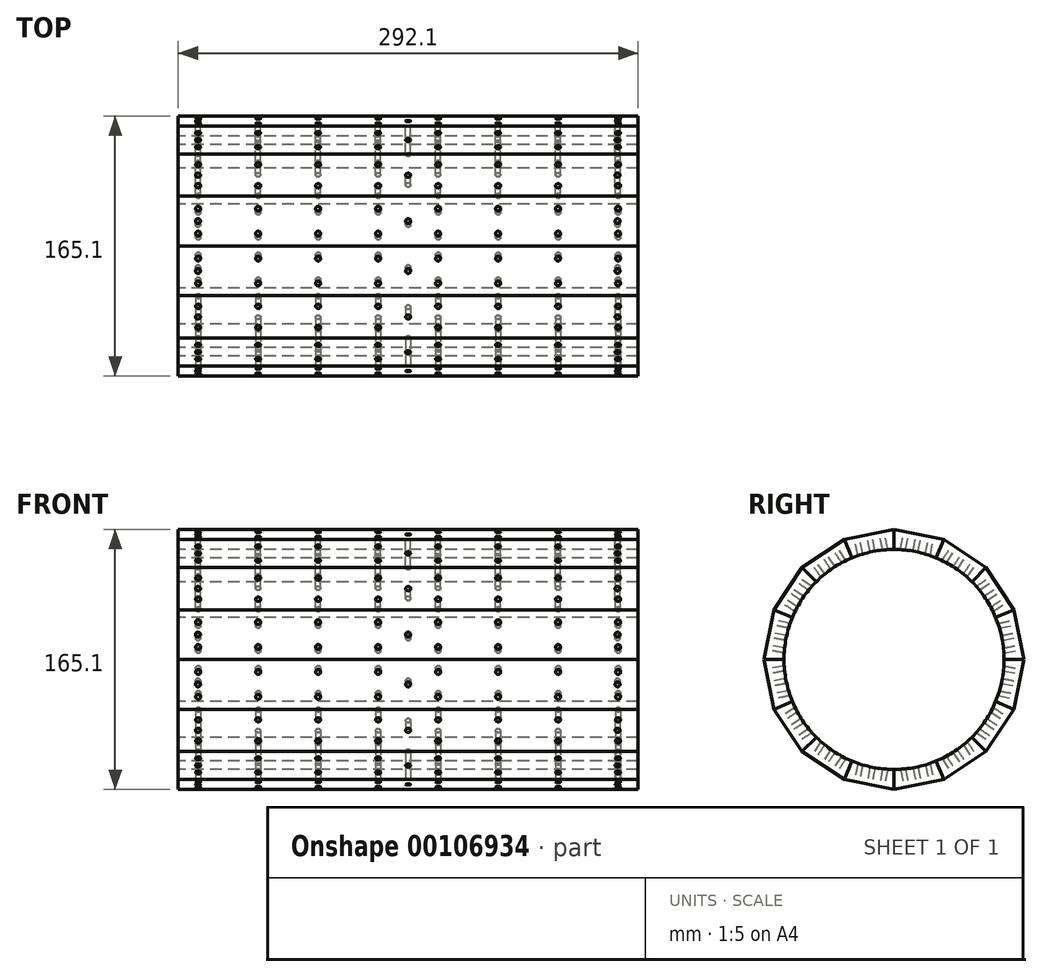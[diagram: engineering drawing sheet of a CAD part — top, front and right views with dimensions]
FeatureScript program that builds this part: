
annotation { "Feature Type Name" : "Feature", "Feature Type Description" : "" }
export const myFeature = defineFeature(function(context is Context, id is Id, definition is map)
    precondition{}
    {
        {
            var Q0;
            Q0=qCreatedBy(makeId("Right.planeOp"),FACE);
            var sketch = newSketch(context, id + "F0", { "sketchPlane" : qUnion([Q0])});
            skCircle(sketch, "E0", {"center": v(0, 0) * mm, "radius": 69.85 * mm, "construction": true});
            skCircle(sketch, "E1", {"center": v(0, 0) * mm, "radius": 82.55 * mm, "construction": true});
            skLineSegment(sketch, "E2.0", {"start": v(0, -82.55) * mm, "end": v(-31.6, -76.27) * mm, "construction": true});
            skLineSegment(sketch, "E2.1", {"start": v(-31.6, -76.27) * mm, "end": v(-58.37, -58.37) * mm, "construction": true});
            skLineSegment(sketch, "E2.2", {"start": v(-58.37, -58.37) * mm, "end": v(-76.27, -31.6) * mm, "construction": true});
            skLineSegment(sketch, "E2.3", {"start": v(-76.27, -31.6) * mm, "end": v(-82.55, 0) * mm, "construction": true});
            skLineSegment(sketch, "E2.4", {"start": v(-82.55, 0) * mm, "end": v(-76.27, 31.6) * mm, "construction": true});
            skLineSegment(sketch, "E2.5", {"start": v(-76.27, 31.6) * mm, "end": v(-58.37, 58.37) * mm, "construction": true});
            skLineSegment(sketch, "E2.6", {"start": v(-58.37, 58.37) * mm, "end": v(-31.6, 76.27) * mm, "construction": true});
            skLineSegment(sketch, "E2.7", {"start": v(-31.6, 76.27) * mm, "end": v(0, 82.55) * mm, "construction": true});
            skLineSegment(sketch, "E2.8", {"start": v(0, 82.55) * mm, "end": v(31.6, 76.27) * mm, "construction": true});
            skLineSegment(sketch, "E2.9", {"start": v(31.6, 76.27) * mm, "end": v(58.37, 58.37) * mm, "construction": true});
            skLineSegment(sketch, "E2.10", {"start": v(58.37, 58.37) * mm, "end": v(76.27, 31.6) * mm, "construction": true});
            skLineSegment(sketch, "E2.11", {"start": v(76.27, 31.6) * mm, "end": v(82.55, 0) * mm, "construction": true});
            skLineSegment(sketch, "E2.12", {"start": v(82.55, 0) * mm, "end": v(76.27, -31.6) * mm, "construction": true});
            skLineSegment(sketch, "E2.13", {"start": v(76.27, -31.6) * mm, "end": v(58.37, -58.37) * mm, "construction": true});
            skLineSegment(sketch, "E2.14", {"start": v(58.37, -58.37) * mm, "end": v(31.6, -76.27) * mm, "construction": true});
            skLineSegment(sketch, "E2.15", {"start": v(31.6, -76.27) * mm, "end": v(0, -82.55) * mm, "construction": true});
            skLineSegment(sketch, "E3", {"start": v(0, -82.55) * mm, "end": v(0, -69.85) * mm, "construction": true});
            skLineSegment(sketch, "E4.1.0", {"start": v(-31.6, -76.27) * mm, "end": v(-26.73, -64.53) * mm, "construction": true});
            skLineSegment(sketch, "E4.2.0", {"start": v(-58.37, -58.37) * mm, "end": v(-49.4, -49.4) * mm, "construction": true});
            skLineSegment(sketch, "E4.3.0", {"start": v(-76.27, -31.6) * mm, "end": v(-64.53, -26.73) * mm, "construction": true});
            skLineSegment(sketch, "E4.4.0", {"start": v(-82.55, 0) * mm, "end": v(-69.85, 0) * mm, "construction": true});
            skLineSegment(sketch, "E4.5.0", {"start": v(-76.27, 31.6) * mm, "end": v(-64.53, 26.73) * mm, "construction": true});
            skLineSegment(sketch, "E4.6.0", {"start": v(-58.37, 58.37) * mm, "end": v(-49.4, 49.4) * mm, "construction": true});
            skLineSegment(sketch, "E4.7.0", {"start": v(-31.6, 76.27) * mm, "end": v(-26.73, 64.53) * mm, "construction": true});
            skLineSegment(sketch, "E4.8.0", {"start": v(0, 82.55) * mm, "end": v(0, 69.85) * mm, "construction": true});
            skLineSegment(sketch, "E4.9.0", {"start": v(31.6, 76.27) * mm, "end": v(26.73, 64.53) * mm, "construction": true});
            skLineSegment(sketch, "E4.10.0", {"start": v(58.37, 58.37) * mm, "end": v(49.4, 49.4) * mm, "construction": true});
            skLineSegment(sketch, "E4.11.0", {"start": v(76.27, 31.6) * mm, "end": v(64.53, 26.73) * mm, "construction": true});
            skLineSegment(sketch, "E4.12.0", {"start": v(82.55, 0) * mm, "end": v(69.85, 0) * mm, "construction": true});
            skLineSegment(sketch, "E4.13.0", {"start": v(76.27, -31.6) * mm, "end": v(64.53, -26.73) * mm, "construction": true});
            skLineSegment(sketch, "E4.14.0", {"start": v(58.37, -58.37) * mm, "end": v(49.4, -49.4) * mm, "construction": true});
            skLineSegment(sketch, "E4.15.0", {"start": v(31.6, -76.27) * mm, "end": v(26.73, -64.53) * mm, "construction": true});
            skLineSegment(sketch, "E4.anchor1", {"start": v(0, -69.85) * mm, "end": v(0, -82.55) * mm, "construction": true});
            skLineSegment(sketch, "E4.anchor2", {"start": v(26.73, -64.53) * mm, "end": v(31.6, -76.27) * mm, "construction": true});
            skLineSegment(sketch, "E5", {"start": v(0, -82.55) * mm, "end": v(-31.6, -76.27) * mm});
            skLineSegment(sketch, "E6", {"start": v(-31.6, -76.27) * mm, "end": v(-26.73, -64.53) * mm});
            skLineSegment(sketch, "E7", {"start": v(0, -82.55) * mm, "end": v(0, -69.85) * mm});
            skArc(sketch, "E8", {"start": v(-26.73, -64.53) * mm, "mid": v(-13.63, -68.5) * mm, "end": v(0, -69.85) * mm});
            skSolve(sketch);
        }
        {
            var Q0;
            Q0=makeQuery(id+"F0.imprint","IMPRINT",FACE,{"disambiguationData":[TD([[makeQuery(id+"F0.imprint","IMPRINT",EDGE,{"derivedFrom":sQuery(id+"F0.wireOp",EDGE,"E5")}),-1.0]])]});
            extrude(context, id + "F1", {"entities" : qUnion([Q0]), "endBound" : BoundingType.SYMMETRIC, "depth" : 292.1 * mm});
        }
        {
            var Q0;
            Q0=qCreatedBy(makeId("Front.planeOp"),FACE);
            var sketch = newSketch(context, id + "F2", { "sketchPlane" : qUnion([Q0])});
            skLineSegment(sketch, "E9", {"start": v(0, 0) * mm, "end": v(152.5, 0) * mm});
            skSolve(sketch);
        }
        {
            var Q0;
            Q0=makeQuery(id+"F1.opExtrude","SWEPT_BODY",BODY,{"disambiguationData":[OSD([sQuery(id+"F0.wireOp",EDGE,"E5"),sQuery(id+"F0.wireOp",EDGE,"E6"),sQuery(id+"F0.wireOp",EDGE,"E7"),sQuery(id+"F0.wireOp",EDGE,"E8")])]});
            var Q1;
            Q1=sQuery(id+"F2.wireOp",EDGE,"E9");
            circularPattern(context, id + "F3", {"entities" : qUnion([Q0]), "axis" : qUnion([Q1]), "angle" : 360 * degree, "instanceCount" : 16, "equalSpace" : true});
        }
        {
            var Q0;
            Q0=makeQuery(id+"F3.opPattern","COPY",FACE,{"derivedFrom":makeQuery(id+"F1.opExtrude","SWEPT_FACE",FACE,{"disambiguationData":[OSD([sQuery(id+"F0.wireOp",EDGE,"E5")])]}),"instanceName":"9"});
            var sketch = newSketch(context, id + "F4", { "sketchPlane" : qUnion([Q0])});
            skLineSegment(sketch, "E10", {"start": v(-133.35, 0) * mm, "end": v(-95.25, 0) * mm, "construction": true});
            skLineSegment(sketch, "E11", {"start": v(-95.25, 0) * mm, "end": v(-57.15, 0) * mm, "construction": true});
            skLineSegment(sketch, "E12", {"start": v(-57.15, 0) * mm, "end": v(-19.05, 0) * mm, "construction": true});
            skLineSegment(sketch, "E13", {"start": v(-19.05, 0) * mm, "end": v(19.05, 0) * mm, "construction": true});
            skLineSegment(sketch, "E14", {"start": v(19.05, 0) * mm, "end": v(57.15, 0) * mm, "construction": true});
            skLineSegment(sketch, "E15", {"start": v(57.15, 0) * mm, "end": v(95.25, 0) * mm, "construction": true});
            skLineSegment(sketch, "E16", {"start": v(95.25, 0) * mm, "end": v(133.35, 0) * mm, "construction": true});
            skLineSegment(sketch, "E17", {"start": v(133.35, 0) * mm, "end": v(146.05, 0) * mm, "construction": true});
            skLineSegment(sketch, "E18", {"start": v(-133.35, 0) * mm, "end": v(-146.05, 0) * mm, "construction": true});
            skLineSegment(sketch, "E19", {"start": v(-133.35, -16.1) * mm, "end": v(-133.35, 16.1) * mm, "construction": true});
            skCircle(sketch, "E20", {"center": v(-133.35, -8.05) * mm, "radius": 1.59 * mm});
            skCircle(sketch, "E21", {"center": v(-133.35, 8.05) * mm, "radius": 1.59 * mm});
            skCircle(sketch, "E22.MirrorC", {"center": v(-133.35, 40.26) * mm, "radius": 1.59 * mm, "construction": true});
            skCircle(sketch, "E23.MirrorC", {"center": v(-133.35, 24.16) * mm, "radius": 1.59 * mm, "construction": true});
            skLineSegment(sketch, "E24", {"start": v(-133.35, -8.05) * mm, "end": v(-133.35, 8.05) * mm, "construction": true});
            skLineSegment(sketch, "E25", {"start": v(-133.35, 24.16) * mm, "end": v(-133.35, 8.05) * mm, "construction": true});
            skLineSegment(sketch, "E26", {"start": v(-133.35, 40.26) * mm, "end": v(-133.35, 24.16) * mm, "construction": true});
            skCircle(sketch, "E27.1.0.0", {"center": v(-95.25, 8.05) * mm, "radius": 1.59 * mm});
            skCircle(sketch, "E27.1.0.1", {"center": v(-95.25, -8.05) * mm, "radius": 1.59 * mm});
            skCircle(sketch, "E27.2.0.0", {"center": v(-57.15, 8.05) * mm, "radius": 1.59 * mm});
            skCircle(sketch, "E27.2.0.1", {"center": v(-57.15, -8.05) * mm, "radius": 1.59 * mm});
            skCircle(sketch, "E27.3.0.0", {"center": v(-19.05, 8.05) * mm, "radius": 1.59 * mm});
            skCircle(sketch, "E27.3.0.1", {"center": v(-19.05, -8.05) * mm, "radius": 1.59 * mm});
            skCircle(sketch, "E27.4.0.0", {"center": v(19.05, 8.05) * mm, "radius": 1.59 * mm});
            skCircle(sketch, "E27.4.0.1", {"center": v(19.05, -8.05) * mm, "radius": 1.59 * mm});
            skCircle(sketch, "E27.5.0.0", {"center": v(57.15, 8.05) * mm, "radius": 1.59 * mm});
            skCircle(sketch, "E27.5.0.1", {"center": v(57.15, -8.05) * mm, "radius": 1.59 * mm});
            skCircle(sketch, "E27.6.0.0", {"center": v(95.25, 8.05) * mm, "radius": 1.59 * mm});
            skCircle(sketch, "E27.6.0.1", {"center": v(95.25, -8.05) * mm, "radius": 1.59 * mm});
            skCircle(sketch, "E27.7.0.0", {"center": v(133.35, 8.05) * mm, "radius": 1.59 * mm});
            skCircle(sketch, "E27.7.0.1", {"center": v(133.35, -8.05) * mm, "radius": 1.59 * mm});
            skLineSegment(sketch, "E27.direction1", {"start": v(-133.35, -8.05) * mm, "end": v(-95.25, -8.05) * mm, "construction": true});
            skSolve(sketch);
        }
        {
            var Q0;
            Q0 = qSketchRegion(id + "F4", true);
            extrude(context, id + "F5", {"entities" : qUnion([Q0]), "oppositeDirection" : true, "depth" : 50.8 * mm});
        }
        {
            var Q0;
            Q0=makeQuery(id+"F5.opExtrude","SWEPT_BODY",BODY,{"disambiguationData":[OSD([sQuery(id+"F4.wireOp",EDGE,"E27.7.0.0")])]});
            var Q1;
            Q1=makeQuery(id+"F5.opExtrude","SWEPT_BODY",BODY,{"disambiguationData":[OSD([sQuery(id+"F4.wireOp",EDGE,"E27.7.0.1")])]});
            var Q2;
            Q2=makeQuery(id+"F5.opExtrude","SWEPT_BODY",BODY,{"disambiguationData":[OSD([sQuery(id+"F4.wireOp",EDGE,"E27.6.0.0")])]});
            var Q3;
            Q3=makeQuery(id+"F5.opExtrude","SWEPT_BODY",BODY,{"disambiguationData":[OSD([sQuery(id+"F4.wireOp",EDGE,"E27.6.0.1")])]});
            var Q4;
            Q4=makeQuery(id+"F5.opExtrude","SWEPT_BODY",BODY,{"disambiguationData":[OSD([sQuery(id+"F4.wireOp",EDGE,"E27.5.0.0")])]});
            var Q5;
            Q5=makeQuery(id+"F5.opExtrude","SWEPT_BODY",BODY,{"disambiguationData":[OSD([sQuery(id+"F4.wireOp",EDGE,"E27.5.0.1")])]});
            var Q6;
            Q6=makeQuery(id+"F5.opExtrude","SWEPT_BODY",BODY,{"disambiguationData":[OSD([sQuery(id+"F4.wireOp",EDGE,"E27.4.0.0")])]});
            var Q7;
            Q7=makeQuery(id+"F5.opExtrude","SWEPT_BODY",BODY,{"disambiguationData":[OSD([sQuery(id+"F4.wireOp",EDGE,"E27.4.0.1")])]});
            var Q8;
            Q8=makeQuery(id+"F5.opExtrude","SWEPT_BODY",BODY,{"disambiguationData":[OSD([sQuery(id+"F4.wireOp",EDGE,"E27.3.0.0")])]});
            var Q9;
            Q9=makeQuery(id+"F5.opExtrude","SWEPT_BODY",BODY,{"disambiguationData":[OSD([sQuery(id+"F4.wireOp",EDGE,"E27.3.0.1")])]});
            var Q10;
            Q10=makeQuery(id+"F5.opExtrude","SWEPT_BODY",BODY,{"disambiguationData":[OSD([sQuery(id+"F4.wireOp",EDGE,"E27.2.0.0")])]});
            var Q11;
            Q11=makeQuery(id+"F5.opExtrude","SWEPT_BODY",BODY,{"disambiguationData":[OSD([sQuery(id+"F4.wireOp",EDGE,"E27.2.0.1")])]});
            var Q12;
            Q12=makeQuery(id+"F5.opExtrude","SWEPT_BODY",BODY,{"disambiguationData":[OSD([sQuery(id+"F4.wireOp",EDGE,"E27.1.0.0")])]});
            var Q13;
            Q13=makeQuery(id+"F5.opExtrude","SWEPT_BODY",BODY,{"disambiguationData":[OSD([sQuery(id+"F4.wireOp",EDGE,"E27.1.0.1")])]});
            var Q14;
            Q14=makeQuery(id+"F5.opExtrude","SWEPT_BODY",BODY,{"disambiguationData":[OSD([sQuery(id+"F4.wireOp",EDGE,"E21")])]});
            var Q15;
            Q15=makeQuery(id+"F5.opExtrude","SWEPT_BODY",BODY,{"disambiguationData":[OSD([sQuery(id+"F4.wireOp",EDGE,"E20")])]});
            var Q16;
            Q16=sQuery(id+"F2.wireOp",EDGE,"E9");
            circularPattern(context, id + "F6", {"entities" : qUnion([Q0, Q1, Q2, Q3, Q4, Q5, Q6, Q7, Q8, Q9, Q10, Q11, Q12, Q13, Q14, Q15]), "axis" : qUnion([Q16]), "angle" : 360 * degree, "instanceCount" : 16, "equalSpace" : true});
        }
        {
            var Q0;
            Q0=makeQuery(id+"F6.opPattern","COPY",BODY,{"derivedFrom":makeQuery(id+"F5.opExtrude","SWEPT_BODY",BODY,{"disambiguationData":[OSD([sQuery(id+"F4.wireOp",EDGE,"E27.7.0.0")])]}),"instanceName":"1"});
            var Q1;
            Q1=makeQuery(id+"F6.opPattern","COPY",BODY,{"derivedFrom":makeQuery(id+"F5.opExtrude","SWEPT_BODY",BODY,{"disambiguationData":[OSD([sQuery(id+"F4.wireOp",EDGE,"E27.7.0.1")])]}),"instanceName":"1"});
            var Q2;
            Q2=makeQuery(id+"F5.opExtrude","SWEPT_BODY",BODY,{"disambiguationData":[OSD([sQuery(id+"F4.wireOp",EDGE,"E27.7.0.0")])]});
            var Q3;
            Q3=makeQuery(id+"F5.opExtrude","SWEPT_BODY",BODY,{"disambiguationData":[OSD([sQuery(id+"F4.wireOp",EDGE,"E27.7.0.1")])]});
            var Q4;
            Q4=makeQuery(id+"F6.opPattern","COPY",BODY,{"derivedFrom":makeQuery(id+"F5.opExtrude","SWEPT_BODY",BODY,{"disambiguationData":[OSD([sQuery(id+"F4.wireOp",EDGE,"E27.7.0.0")])]}),"instanceName":"2"});
            var Q5;
            Q5=makeQuery(id+"F6.opPattern","COPY",BODY,{"derivedFrom":makeQuery(id+"F5.opExtrude","SWEPT_BODY",BODY,{"disambiguationData":[OSD([sQuery(id+"F4.wireOp",EDGE,"E27.7.0.1")])]}),"instanceName":"2"});
            var Q6;
            Q6=makeQuery(id+"F6.opPattern","COPY",BODY,{"derivedFrom":makeQuery(id+"F5.opExtrude","SWEPT_BODY",BODY,{"disambiguationData":[OSD([sQuery(id+"F4.wireOp",EDGE,"E27.7.0.0")])]}),"instanceName":"3"});
            var Q7;
            Q7=makeQuery(id+"F6.opPattern","COPY",BODY,{"derivedFrom":makeQuery(id+"F5.opExtrude","SWEPT_BODY",BODY,{"disambiguationData":[OSD([sQuery(id+"F4.wireOp",EDGE,"E27.7.0.1")])]}),"instanceName":"3"});
            var Q8;
            Q8=makeQuery(id+"F6.opPattern","COPY",BODY,{"derivedFrom":makeQuery(id+"F5.opExtrude","SWEPT_BODY",BODY,{"disambiguationData":[OSD([sQuery(id+"F4.wireOp",EDGE,"E27.7.0.0")])]}),"instanceName":"4"});
            var Q9;
            Q9=makeQuery(id+"F6.opPattern","COPY",BODY,{"derivedFrom":makeQuery(id+"F5.opExtrude","SWEPT_BODY",BODY,{"disambiguationData":[OSD([sQuery(id+"F4.wireOp",EDGE,"E27.7.0.1")])]}),"instanceName":"4"});
            var Q10;
            Q10=makeQuery(id+"F6.opPattern","COPY",BODY,{"derivedFrom":makeQuery(id+"F5.opExtrude","SWEPT_BODY",BODY,{"disambiguationData":[OSD([sQuery(id+"F4.wireOp",EDGE,"E27.7.0.0")])]}),"instanceName":"5"});
            var Q11;
            Q11=makeQuery(id+"F6.opPattern","COPY",BODY,{"derivedFrom":makeQuery(id+"F5.opExtrude","SWEPT_BODY",BODY,{"disambiguationData":[OSD([sQuery(id+"F4.wireOp",EDGE,"E27.7.0.1")])]}),"instanceName":"5"});
            var Q12;
            Q12=makeQuery(id+"F6.opPattern","COPY",BODY,{"derivedFrom":makeQuery(id+"F5.opExtrude","SWEPT_BODY",BODY,{"disambiguationData":[OSD([sQuery(id+"F4.wireOp",EDGE,"E27.7.0.0")])]}),"instanceName":"6"});
            var Q13;
            Q13=makeQuery(id+"F6.opPattern","COPY",BODY,{"derivedFrom":makeQuery(id+"F5.opExtrude","SWEPT_BODY",BODY,{"disambiguationData":[OSD([sQuery(id+"F4.wireOp",EDGE,"E27.7.0.1")])]}),"instanceName":"6"});
            var Q14;
            Q14=makeQuery(id+"F6.opPattern","COPY",BODY,{"derivedFrom":makeQuery(id+"F5.opExtrude","SWEPT_BODY",BODY,{"disambiguationData":[OSD([sQuery(id+"F4.wireOp",EDGE,"E27.7.0.0")])]}),"instanceName":"7"});
            var Q15;
            Q15=makeQuery(id+"F6.opPattern","COPY",BODY,{"derivedFrom":makeQuery(id+"F5.opExtrude","SWEPT_BODY",BODY,{"disambiguationData":[OSD([sQuery(id+"F4.wireOp",EDGE,"E27.7.0.1")])]}),"instanceName":"8"});
            var Q16;
            Q16=makeQuery(id+"F6.opPattern","COPY",BODY,{"derivedFrom":makeQuery(id+"F5.opExtrude","SWEPT_BODY",BODY,{"disambiguationData":[OSD([sQuery(id+"F4.wireOp",EDGE,"E27.7.0.0")])]}),"instanceName":"9"});
            var Q17;
            Q17=makeQuery(id+"F6.opPattern","COPY",BODY,{"derivedFrom":makeQuery(id+"F5.opExtrude","SWEPT_BODY",BODY,{"disambiguationData":[OSD([sQuery(id+"F4.wireOp",EDGE,"E27.7.0.1")])]}),"instanceName":"9"});
            var Q18;
            Q18=makeQuery(id+"F6.opPattern","COPY",BODY,{"derivedFrom":makeQuery(id+"F5.opExtrude","SWEPT_BODY",BODY,{"disambiguationData":[OSD([sQuery(id+"F4.wireOp",EDGE,"E27.7.0.0")])]}),"instanceName":"10"});
            var Q19;
            Q19=makeQuery(id+"F6.opPattern","COPY",BODY,{"derivedFrom":makeQuery(id+"F5.opExtrude","SWEPT_BODY",BODY,{"disambiguationData":[OSD([sQuery(id+"F4.wireOp",EDGE,"E27.7.0.1")])]}),"instanceName":"10"});
            var Q20;
            Q20=makeQuery(id+"F6.opPattern","COPY",BODY,{"derivedFrom":makeQuery(id+"F5.opExtrude","SWEPT_BODY",BODY,{"disambiguationData":[OSD([sQuery(id+"F4.wireOp",EDGE,"E27.7.0.0")])]}),"instanceName":"11"});
            var Q21;
            Q21=makeQuery(id+"F6.opPattern","COPY",BODY,{"derivedFrom":makeQuery(id+"F5.opExtrude","SWEPT_BODY",BODY,{"disambiguationData":[OSD([sQuery(id+"F4.wireOp",EDGE,"E27.7.0.1")])]}),"instanceName":"11"});
            var Q22;
            Q22=makeQuery(id+"F6.opPattern","COPY",BODY,{"derivedFrom":makeQuery(id+"F5.opExtrude","SWEPT_BODY",BODY,{"disambiguationData":[OSD([sQuery(id+"F4.wireOp",EDGE,"E27.7.0.0")])]}),"instanceName":"12"});
            var Q23;
            Q23=makeQuery(id+"F6.opPattern","COPY",BODY,{"derivedFrom":makeQuery(id+"F5.opExtrude","SWEPT_BODY",BODY,{"disambiguationData":[OSD([sQuery(id+"F4.wireOp",EDGE,"E27.7.0.1")])]}),"instanceName":"12"});
            var Q24;
            Q24=makeQuery(id+"F6.opPattern","COPY",BODY,{"derivedFrom":makeQuery(id+"F5.opExtrude","SWEPT_BODY",BODY,{"disambiguationData":[OSD([sQuery(id+"F4.wireOp",EDGE,"E27.7.0.0")])]}),"instanceName":"13"});
            var Q25;
            Q25=makeQuery(id+"F6.opPattern","COPY",BODY,{"derivedFrom":makeQuery(id+"F5.opExtrude","SWEPT_BODY",BODY,{"disambiguationData":[OSD([sQuery(id+"F4.wireOp",EDGE,"E27.7.0.1")])]}),"instanceName":"13"});
            var Q26;
            Q26=makeQuery(id+"F6.opPattern","COPY",BODY,{"derivedFrom":makeQuery(id+"F5.opExtrude","SWEPT_BODY",BODY,{"disambiguationData":[OSD([sQuery(id+"F4.wireOp",EDGE,"E27.7.0.0")])]}),"instanceName":"14"});
            var Q27;
            Q27=makeQuery(id+"F6.opPattern","COPY",BODY,{"derivedFrom":makeQuery(id+"F5.opExtrude","SWEPT_BODY",BODY,{"disambiguationData":[OSD([sQuery(id+"F4.wireOp",EDGE,"E27.7.0.1")])]}),"instanceName":"14"});
            var Q28;
            Q28=makeQuery(id+"F6.opPattern","COPY",BODY,{"derivedFrom":makeQuery(id+"F5.opExtrude","SWEPT_BODY",BODY,{"disambiguationData":[OSD([sQuery(id+"F4.wireOp",EDGE,"E27.7.0.0")])]}),"instanceName":"15"});
            var Q29;
            Q29=makeQuery(id+"F6.opPattern","COPY",BODY,{"derivedFrom":makeQuery(id+"F5.opExtrude","SWEPT_BODY",BODY,{"disambiguationData":[OSD([sQuery(id+"F4.wireOp",EDGE,"E27.7.0.1")])]}),"instanceName":"15"});
            var Q30;
            Q30=makeQuery(id+"F5.opExtrude","SWEPT_BODY",BODY,{"disambiguationData":[OSD([sQuery(id+"F4.wireOp",EDGE,"E27.6.0.1")])]});
            var Q31;
            Q31=makeQuery(id+"F5.opExtrude","SWEPT_BODY",BODY,{"disambiguationData":[OSD([sQuery(id+"F4.wireOp",EDGE,"E27.6.0.0")])]});
            var Q32;
            Q32=makeQuery(id+"F6.opPattern","COPY",BODY,{"derivedFrom":makeQuery(id+"F5.opExtrude","SWEPT_BODY",BODY,{"disambiguationData":[OSD([sQuery(id+"F4.wireOp",EDGE,"E27.6.0.1")])]}),"instanceName":"1"});
            var Q33;
            Q33=makeQuery(id+"F6.opPattern","COPY",BODY,{"derivedFrom":makeQuery(id+"F5.opExtrude","SWEPT_BODY",BODY,{"disambiguationData":[OSD([sQuery(id+"F4.wireOp",EDGE,"E27.6.0.0")])]}),"instanceName":"1"});
            var Q34;
            Q34=makeQuery(id+"F6.opPattern","COPY",BODY,{"derivedFrom":makeQuery(id+"F5.opExtrude","SWEPT_BODY",BODY,{"disambiguationData":[OSD([sQuery(id+"F4.wireOp",EDGE,"E27.6.0.0")])]}),"instanceName":"2"});
            var Q35;
            Q35=makeQuery(id+"F6.opPattern","COPY",BODY,{"derivedFrom":makeQuery(id+"F5.opExtrude","SWEPT_BODY",BODY,{"disambiguationData":[OSD([sQuery(id+"F4.wireOp",EDGE,"E27.6.0.1")])]}),"instanceName":"2"});
            var Q36;
            Q36=makeQuery(id+"F6.opPattern","COPY",BODY,{"derivedFrom":makeQuery(id+"F5.opExtrude","SWEPT_BODY",BODY,{"disambiguationData":[OSD([sQuery(id+"F4.wireOp",EDGE,"E27.6.0.0")])]}),"instanceName":"3"});
            var Q37;
            Q37=makeQuery(id+"F6.opPattern","COPY",BODY,{"derivedFrom":makeQuery(id+"F5.opExtrude","SWEPT_BODY",BODY,{"disambiguationData":[OSD([sQuery(id+"F4.wireOp",EDGE,"E27.6.0.1")])]}),"instanceName":"3"});
            var Q38;
            Q38=makeQuery(id+"F6.opPattern","COPY",BODY,{"derivedFrom":makeQuery(id+"F5.opExtrude","SWEPT_BODY",BODY,{"disambiguationData":[OSD([sQuery(id+"F4.wireOp",EDGE,"E27.6.0.0")])]}),"instanceName":"4"});
            var Q39;
            Q39=makeQuery(id+"F6.opPattern","COPY",BODY,{"derivedFrom":makeQuery(id+"F5.opExtrude","SWEPT_BODY",BODY,{"disambiguationData":[OSD([sQuery(id+"F4.wireOp",EDGE,"E27.6.0.1")])]}),"instanceName":"4"});
            var Q40;
            Q40=makeQuery(id+"F6.opPattern","COPY",BODY,{"derivedFrom":makeQuery(id+"F5.opExtrude","SWEPT_BODY",BODY,{"disambiguationData":[OSD([sQuery(id+"F4.wireOp",EDGE,"E27.6.0.0")])]}),"instanceName":"5"});
            var Q41;
            Q41=makeQuery(id+"F6.opPattern","COPY",BODY,{"derivedFrom":makeQuery(id+"F5.opExtrude","SWEPT_BODY",BODY,{"disambiguationData":[OSD([sQuery(id+"F4.wireOp",EDGE,"E27.6.0.1")])]}),"instanceName":"5"});
            var Q42;
            Q42=makeQuery(id+"F6.opPattern","COPY",BODY,{"derivedFrom":makeQuery(id+"F5.opExtrude","SWEPT_BODY",BODY,{"disambiguationData":[OSD([sQuery(id+"F4.wireOp",EDGE,"E27.6.0.0")])]}),"instanceName":"6"});
            var Q43;
            Q43=makeQuery(id+"F6.opPattern","COPY",BODY,{"derivedFrom":makeQuery(id+"F5.opExtrude","SWEPT_BODY",BODY,{"disambiguationData":[OSD([sQuery(id+"F4.wireOp",EDGE,"E27.6.0.0")])]}),"instanceName":"7"});
            var Q44;
            Q44=makeQuery(id+"F6.opPattern","COPY",BODY,{"derivedFrom":makeQuery(id+"F5.opExtrude","SWEPT_BODY",BODY,{"disambiguationData":[OSD([sQuery(id+"F4.wireOp",EDGE,"E27.6.0.1")])]}),"instanceName":"8"});
            var Q45;
            Q45=makeQuery(id+"F6.opPattern","COPY",BODY,{"derivedFrom":makeQuery(id+"F5.opExtrude","SWEPT_BODY",BODY,{"disambiguationData":[OSD([sQuery(id+"F4.wireOp",EDGE,"E27.6.0.0")])]}),"instanceName":"9"});
            var Q46;
            Q46=makeQuery(id+"F6.opPattern","COPY",BODY,{"derivedFrom":makeQuery(id+"F5.opExtrude","SWEPT_BODY",BODY,{"disambiguationData":[OSD([sQuery(id+"F4.wireOp",EDGE,"E27.6.0.1")])]}),"instanceName":"9"});
            var Q47;
            Q47=makeQuery(id+"F6.opPattern","COPY",BODY,{"derivedFrom":makeQuery(id+"F5.opExtrude","SWEPT_BODY",BODY,{"disambiguationData":[OSD([sQuery(id+"F4.wireOp",EDGE,"E27.6.0.0")])]}),"instanceName":"10"});
            var Q48;
            Q48=makeQuery(id+"F6.opPattern","COPY",BODY,{"derivedFrom":makeQuery(id+"F5.opExtrude","SWEPT_BODY",BODY,{"disambiguationData":[OSD([sQuery(id+"F4.wireOp",EDGE,"E27.6.0.1")])]}),"instanceName":"10"});
            var Q49;
            Q49=makeQuery(id+"F6.opPattern","COPY",BODY,{"derivedFrom":makeQuery(id+"F5.opExtrude","SWEPT_BODY",BODY,{"disambiguationData":[OSD([sQuery(id+"F4.wireOp",EDGE,"E27.6.0.0")])]}),"instanceName":"11"});
            var Q50;
            Q50=makeQuery(id+"F6.opPattern","COPY",BODY,{"derivedFrom":makeQuery(id+"F5.opExtrude","SWEPT_BODY",BODY,{"disambiguationData":[OSD([sQuery(id+"F4.wireOp",EDGE,"E27.6.0.1")])]}),"instanceName":"11"});
            var Q51;
            Q51=makeQuery(id+"F6.opPattern","COPY",BODY,{"derivedFrom":makeQuery(id+"F5.opExtrude","SWEPT_BODY",BODY,{"disambiguationData":[OSD([sQuery(id+"F4.wireOp",EDGE,"E27.6.0.0")])]}),"instanceName":"12"});
            var Q52;
            Q52=makeQuery(id+"F6.opPattern","COPY",BODY,{"derivedFrom":makeQuery(id+"F5.opExtrude","SWEPT_BODY",BODY,{"disambiguationData":[OSD([sQuery(id+"F4.wireOp",EDGE,"E27.6.0.1")])]}),"instanceName":"12"});
            var Q53;
            Q53=makeQuery(id+"F6.opPattern","COPY",BODY,{"derivedFrom":makeQuery(id+"F5.opExtrude","SWEPT_BODY",BODY,{"disambiguationData":[OSD([sQuery(id+"F4.wireOp",EDGE,"E27.6.0.0")])]}),"instanceName":"13"});
            var Q54;
            Q54=makeQuery(id+"F6.opPattern","COPY",BODY,{"derivedFrom":makeQuery(id+"F5.opExtrude","SWEPT_BODY",BODY,{"disambiguationData":[OSD([sQuery(id+"F4.wireOp",EDGE,"E27.6.0.1")])]}),"instanceName":"13"});
            var Q55;
            Q55=makeQuery(id+"F6.opPattern","COPY",BODY,{"derivedFrom":makeQuery(id+"F5.opExtrude","SWEPT_BODY",BODY,{"disambiguationData":[OSD([sQuery(id+"F4.wireOp",EDGE,"E27.6.0.0")])]}),"instanceName":"14"});
            var Q56;
            Q56=makeQuery(id+"F6.opPattern","COPY",BODY,{"derivedFrom":makeQuery(id+"F5.opExtrude","SWEPT_BODY",BODY,{"disambiguationData":[OSD([sQuery(id+"F4.wireOp",EDGE,"E27.6.0.1")])]}),"instanceName":"14"});
            var Q57;
            Q57=makeQuery(id+"F6.opPattern","COPY",BODY,{"derivedFrom":makeQuery(id+"F5.opExtrude","SWEPT_BODY",BODY,{"disambiguationData":[OSD([sQuery(id+"F4.wireOp",EDGE,"E27.6.0.0")])]}),"instanceName":"15"});
            var Q58;
            Q58=makeQuery(id+"F6.opPattern","COPY",BODY,{"derivedFrom":makeQuery(id+"F5.opExtrude","SWEPT_BODY",BODY,{"disambiguationData":[OSD([sQuery(id+"F4.wireOp",EDGE,"E27.6.0.1")])]}),"instanceName":"15"});
            var Q59;
            Q59=makeQuery(id+"F5.opExtrude","SWEPT_BODY",BODY,{"disambiguationData":[OSD([sQuery(id+"F4.wireOp",EDGE,"E27.5.0.0")])]});
            var Q60;
            Q60=makeQuery(id+"F5.opExtrude","SWEPT_BODY",BODY,{"disambiguationData":[OSD([sQuery(id+"F4.wireOp",EDGE,"E27.5.0.1")])]});
            var Q61;
            Q61=makeQuery(id+"F6.opPattern","COPY",BODY,{"derivedFrom":makeQuery(id+"F5.opExtrude","SWEPT_BODY",BODY,{"disambiguationData":[OSD([sQuery(id+"F4.wireOp",EDGE,"E27.5.0.1")])]}),"instanceName":"1"});
            var Q62;
            Q62=makeQuery(id+"F6.opPattern","COPY",BODY,{"derivedFrom":makeQuery(id+"F5.opExtrude","SWEPT_BODY",BODY,{"disambiguationData":[OSD([sQuery(id+"F4.wireOp",EDGE,"E27.5.0.0")])]}),"instanceName":"1"});
            var Q63;
            Q63=makeQuery(id+"F6.opPattern","COPY",BODY,{"derivedFrom":makeQuery(id+"F5.opExtrude","SWEPT_BODY",BODY,{"disambiguationData":[OSD([sQuery(id+"F4.wireOp",EDGE,"E27.5.0.0")])]}),"instanceName":"2"});
            var Q64;
            Q64=makeQuery(id+"F6.opPattern","COPY",BODY,{"derivedFrom":makeQuery(id+"F5.opExtrude","SWEPT_BODY",BODY,{"disambiguationData":[OSD([sQuery(id+"F4.wireOp",EDGE,"E27.5.0.1")])]}),"instanceName":"2"});
            var Q65;
            Q65=makeQuery(id+"F6.opPattern","COPY",BODY,{"derivedFrom":makeQuery(id+"F5.opExtrude","SWEPT_BODY",BODY,{"disambiguationData":[OSD([sQuery(id+"F4.wireOp",EDGE,"E27.5.0.0")])]}),"instanceName":"3"});
            var Q66;
            Q66=makeQuery(id+"F6.opPattern","COPY",BODY,{"derivedFrom":makeQuery(id+"F5.opExtrude","SWEPT_BODY",BODY,{"disambiguationData":[OSD([sQuery(id+"F4.wireOp",EDGE,"E27.5.0.1")])]}),"instanceName":"3"});
            var Q67;
            Q67=makeQuery(id+"F6.opPattern","COPY",BODY,{"derivedFrom":makeQuery(id+"F5.opExtrude","SWEPT_BODY",BODY,{"disambiguationData":[OSD([sQuery(id+"F4.wireOp",EDGE,"E27.5.0.0")])]}),"instanceName":"4"});
            var Q68;
            Q68=makeQuery(id+"F6.opPattern","COPY",BODY,{"derivedFrom":makeQuery(id+"F5.opExtrude","SWEPT_BODY",BODY,{"disambiguationData":[OSD([sQuery(id+"F4.wireOp",EDGE,"E27.5.0.1")])]}),"instanceName":"4"});
            var Q69;
            Q69=makeQuery(id+"F6.opPattern","COPY",BODY,{"derivedFrom":makeQuery(id+"F5.opExtrude","SWEPT_BODY",BODY,{"disambiguationData":[OSD([sQuery(id+"F4.wireOp",EDGE,"E27.5.0.0")])]}),"instanceName":"5"});
            var Q70;
            Q70=makeQuery(id+"F6.opPattern","COPY",BODY,{"derivedFrom":makeQuery(id+"F5.opExtrude","SWEPT_BODY",BODY,{"disambiguationData":[OSD([sQuery(id+"F4.wireOp",EDGE,"E27.5.0.1")])]}),"instanceName":"5"});
            var Q71;
            Q71=makeQuery(id+"F6.opPattern","COPY",BODY,{"derivedFrom":makeQuery(id+"F5.opExtrude","SWEPT_BODY",BODY,{"disambiguationData":[OSD([sQuery(id+"F4.wireOp",EDGE,"E27.5.0.0")])]}),"instanceName":"6"});
            var Q72;
            Q72=makeQuery(id+"F6.opPattern","COPY",BODY,{"derivedFrom":makeQuery(id+"F5.opExtrude","SWEPT_BODY",BODY,{"disambiguationData":[OSD([sQuery(id+"F4.wireOp",EDGE,"E27.6.0.1")])]}),"instanceName":"6"});
            var Q73;
            Q73=makeQuery(id+"F6.opPattern","COPY",BODY,{"derivedFrom":makeQuery(id+"F5.opExtrude","SWEPT_BODY",BODY,{"disambiguationData":[OSD([sQuery(id+"F4.wireOp",EDGE,"E27.5.0.0")])]}),"instanceName":"7"});
            var Q74;
            Q74=makeQuery(id+"F6.opPattern","COPY",BODY,{"derivedFrom":makeQuery(id+"F5.opExtrude","SWEPT_BODY",BODY,{"disambiguationData":[OSD([sQuery(id+"F4.wireOp",EDGE,"E27.5.0.1")])]}),"instanceName":"8"});
            var Q75;
            Q75=makeQuery(id+"F6.opPattern","COPY",BODY,{"derivedFrom":makeQuery(id+"F5.opExtrude","SWEPT_BODY",BODY,{"disambiguationData":[OSD([sQuery(id+"F4.wireOp",EDGE,"E27.5.0.0")])]}),"instanceName":"9"});
            var Q76;
            Q76=makeQuery(id+"F6.opPattern","COPY",BODY,{"derivedFrom":makeQuery(id+"F5.opExtrude","SWEPT_BODY",BODY,{"disambiguationData":[OSD([sQuery(id+"F4.wireOp",EDGE,"E27.5.0.1")])]}),"instanceName":"9"});
            var Q77;
            Q77=makeQuery(id+"F6.opPattern","COPY",BODY,{"derivedFrom":makeQuery(id+"F5.opExtrude","SWEPT_BODY",BODY,{"disambiguationData":[OSD([sQuery(id+"F4.wireOp",EDGE,"E27.5.0.0")])]}),"instanceName":"10"});
            var Q78;
            Q78=makeQuery(id+"F6.opPattern","COPY",BODY,{"derivedFrom":makeQuery(id+"F5.opExtrude","SWEPT_BODY",BODY,{"disambiguationData":[OSD([sQuery(id+"F4.wireOp",EDGE,"E27.5.0.1")])]}),"instanceName":"10"});
            var Q79;
            Q79=makeQuery(id+"F6.opPattern","COPY",BODY,{"derivedFrom":makeQuery(id+"F5.opExtrude","SWEPT_BODY",BODY,{"disambiguationData":[OSD([sQuery(id+"F4.wireOp",EDGE,"E27.5.0.0")])]}),"instanceName":"11"});
            var Q80;
            Q80=makeQuery(id+"F6.opPattern","COPY",BODY,{"derivedFrom":makeQuery(id+"F5.opExtrude","SWEPT_BODY",BODY,{"disambiguationData":[OSD([sQuery(id+"F4.wireOp",EDGE,"E27.5.0.1")])]}),"instanceName":"11"});
            var Q81;
            Q81=makeQuery(id+"F6.opPattern","COPY",BODY,{"derivedFrom":makeQuery(id+"F5.opExtrude","SWEPT_BODY",BODY,{"disambiguationData":[OSD([sQuery(id+"F4.wireOp",EDGE,"E27.5.0.0")])]}),"instanceName":"12"});
            var Q82;
            Q82=makeQuery(id+"F6.opPattern","COPY",BODY,{"derivedFrom":makeQuery(id+"F5.opExtrude","SWEPT_BODY",BODY,{"disambiguationData":[OSD([sQuery(id+"F4.wireOp",EDGE,"E27.5.0.1")])]}),"instanceName":"12"});
            var Q83;
            Q83=makeQuery(id+"F6.opPattern","COPY",BODY,{"derivedFrom":makeQuery(id+"F5.opExtrude","SWEPT_BODY",BODY,{"disambiguationData":[OSD([sQuery(id+"F4.wireOp",EDGE,"E27.5.0.0")])]}),"instanceName":"13"});
            var Q84;
            Q84=makeQuery(id+"F6.opPattern","COPY",BODY,{"derivedFrom":makeQuery(id+"F5.opExtrude","SWEPT_BODY",BODY,{"disambiguationData":[OSD([sQuery(id+"F4.wireOp",EDGE,"E27.5.0.1")])]}),"instanceName":"13"});
            var Q85;
            Q85=makeQuery(id+"F6.opPattern","COPY",BODY,{"derivedFrom":makeQuery(id+"F5.opExtrude","SWEPT_BODY",BODY,{"disambiguationData":[OSD([sQuery(id+"F4.wireOp",EDGE,"E27.5.0.0")])]}),"instanceName":"14"});
            var Q86;
            Q86=makeQuery(id+"F6.opPattern","COPY",BODY,{"derivedFrom":makeQuery(id+"F5.opExtrude","SWEPT_BODY",BODY,{"disambiguationData":[OSD([sQuery(id+"F4.wireOp",EDGE,"E27.5.0.1")])]}),"instanceName":"14"});
            var Q87;
            Q87=makeQuery(id+"F6.opPattern","COPY",BODY,{"derivedFrom":makeQuery(id+"F5.opExtrude","SWEPT_BODY",BODY,{"disambiguationData":[OSD([sQuery(id+"F4.wireOp",EDGE,"E27.5.0.0")])]}),"instanceName":"15"});
            var Q88;
            Q88=makeQuery(id+"F6.opPattern","COPY",BODY,{"derivedFrom":makeQuery(id+"F5.opExtrude","SWEPT_BODY",BODY,{"disambiguationData":[OSD([sQuery(id+"F4.wireOp",EDGE,"E27.5.0.1")])]}),"instanceName":"15"});
            var Q89;
            Q89=makeQuery(id+"F5.opExtrude","SWEPT_BODY",BODY,{"disambiguationData":[OSD([sQuery(id+"F4.wireOp",EDGE,"E27.4.0.0")])]});
            var Q90;
            Q90=makeQuery(id+"F5.opExtrude","SWEPT_BODY",BODY,{"disambiguationData":[OSD([sQuery(id+"F4.wireOp",EDGE,"E27.4.0.1")])]});
            var Q91;
            Q91=makeQuery(id+"F6.opPattern","COPY",BODY,{"derivedFrom":makeQuery(id+"F5.opExtrude","SWEPT_BODY",BODY,{"disambiguationData":[OSD([sQuery(id+"F4.wireOp",EDGE,"E27.4.0.1")])]}),"instanceName":"1"});
            var Q92;
            Q92=makeQuery(id+"F6.opPattern","COPY",BODY,{"derivedFrom":makeQuery(id+"F5.opExtrude","SWEPT_BODY",BODY,{"disambiguationData":[OSD([sQuery(id+"F4.wireOp",EDGE,"E27.4.0.0")])]}),"instanceName":"1"});
            var Q93;
            Q93=makeQuery(id+"F6.opPattern","COPY",BODY,{"derivedFrom":makeQuery(id+"F5.opExtrude","SWEPT_BODY",BODY,{"disambiguationData":[OSD([sQuery(id+"F4.wireOp",EDGE,"E27.4.0.0")])]}),"instanceName":"2"});
            var Q94;
            Q94=makeQuery(id+"F6.opPattern","COPY",BODY,{"derivedFrom":makeQuery(id+"F5.opExtrude","SWEPT_BODY",BODY,{"disambiguationData":[OSD([sQuery(id+"F4.wireOp",EDGE,"E27.4.0.1")])]}),"instanceName":"2"});
            var Q95;
            Q95=makeQuery(id+"F6.opPattern","COPY",BODY,{"derivedFrom":makeQuery(id+"F5.opExtrude","SWEPT_BODY",BODY,{"disambiguationData":[OSD([sQuery(id+"F4.wireOp",EDGE,"E27.4.0.0")])]}),"instanceName":"3"});
            var Q96;
            Q96=makeQuery(id+"F6.opPattern","COPY",BODY,{"derivedFrom":makeQuery(id+"F5.opExtrude","SWEPT_BODY",BODY,{"disambiguationData":[OSD([sQuery(id+"F4.wireOp",EDGE,"E27.4.0.1")])]}),"instanceName":"3"});
            var Q97;
            Q97=makeQuery(id+"F6.opPattern","COPY",BODY,{"derivedFrom":makeQuery(id+"F5.opExtrude","SWEPT_BODY",BODY,{"disambiguationData":[OSD([sQuery(id+"F4.wireOp",EDGE,"E27.4.0.0")])]}),"instanceName":"4"});
            var Q98;
            Q98=makeQuery(id+"F6.opPattern","COPY",BODY,{"derivedFrom":makeQuery(id+"F5.opExtrude","SWEPT_BODY",BODY,{"disambiguationData":[OSD([sQuery(id+"F4.wireOp",EDGE,"E27.4.0.1")])]}),"instanceName":"4"});
            var Q99;
            Q99=makeQuery(id+"F6.opPattern","COPY",BODY,{"derivedFrom":makeQuery(id+"F5.opExtrude","SWEPT_BODY",BODY,{"disambiguationData":[OSD([sQuery(id+"F4.wireOp",EDGE,"E27.4.0.0")])]}),"instanceName":"5"});
            var Q100;
            Q100=makeQuery(id+"F6.opPattern","COPY",BODY,{"derivedFrom":makeQuery(id+"F5.opExtrude","SWEPT_BODY",BODY,{"disambiguationData":[OSD([sQuery(id+"F4.wireOp",EDGE,"E27.4.0.1")])]}),"instanceName":"5"});
            var Q101;
            Q101=makeQuery(id+"F6.opPattern","COPY",BODY,{"derivedFrom":makeQuery(id+"F5.opExtrude","SWEPT_BODY",BODY,{"disambiguationData":[OSD([sQuery(id+"F4.wireOp",EDGE,"E27.4.0.0")])]}),"instanceName":"6"});
            var Q102;
            Q102=makeQuery(id+"F6.opPattern","COPY",BODY,{"derivedFrom":makeQuery(id+"F5.opExtrude","SWEPT_BODY",BODY,{"disambiguationData":[OSD([sQuery(id+"F4.wireOp",EDGE,"E27.4.0.0")])]}),"instanceName":"7"});
            var Q103;
            Q103=makeQuery(id+"F6.opPattern","COPY",BODY,{"derivedFrom":makeQuery(id+"F5.opExtrude","SWEPT_BODY",BODY,{"disambiguationData":[OSD([sQuery(id+"F4.wireOp",EDGE,"E27.4.0.1")])]}),"instanceName":"8"});
            var Q104;
            Q104=makeQuery(id+"F6.opPattern","COPY",BODY,{"derivedFrom":makeQuery(id+"F5.opExtrude","SWEPT_BODY",BODY,{"disambiguationData":[OSD([sQuery(id+"F4.wireOp",EDGE,"E27.4.0.0")])]}),"instanceName":"9"});
            var Q105;
            Q105=makeQuery(id+"F6.opPattern","COPY",BODY,{"derivedFrom":makeQuery(id+"F5.opExtrude","SWEPT_BODY",BODY,{"disambiguationData":[OSD([sQuery(id+"F4.wireOp",EDGE,"E27.4.0.1")])]}),"instanceName":"9"});
            var Q106;
            Q106=makeQuery(id+"F6.opPattern","COPY",BODY,{"derivedFrom":makeQuery(id+"F5.opExtrude","SWEPT_BODY",BODY,{"disambiguationData":[OSD([sQuery(id+"F4.wireOp",EDGE,"E27.4.0.0")])]}),"instanceName":"10"});
            var Q107;
            Q107=makeQuery(id+"F6.opPattern","COPY",BODY,{"derivedFrom":makeQuery(id+"F5.opExtrude","SWEPT_BODY",BODY,{"disambiguationData":[OSD([sQuery(id+"F4.wireOp",EDGE,"E27.4.0.1")])]}),"instanceName":"10"});
            var Q108;
            Q108=makeQuery(id+"F6.opPattern","COPY",BODY,{"derivedFrom":makeQuery(id+"F5.opExtrude","SWEPT_BODY",BODY,{"disambiguationData":[OSD([sQuery(id+"F4.wireOp",EDGE,"E27.4.0.0")])]}),"instanceName":"11"});
            var Q109;
            Q109=makeQuery(id+"F6.opPattern","COPY",BODY,{"derivedFrom":makeQuery(id+"F5.opExtrude","SWEPT_BODY",BODY,{"disambiguationData":[OSD([sQuery(id+"F4.wireOp",EDGE,"E27.4.0.1")])]}),"instanceName":"11"});
            var Q110;
            Q110=makeQuery(id+"F6.opPattern","COPY",BODY,{"derivedFrom":makeQuery(id+"F5.opExtrude","SWEPT_BODY",BODY,{"disambiguationData":[OSD([sQuery(id+"F4.wireOp",EDGE,"E27.4.0.0")])]}),"instanceName":"12"});
            var Q111;
            Q111=makeQuery(id+"F6.opPattern","COPY",BODY,{"derivedFrom":makeQuery(id+"F5.opExtrude","SWEPT_BODY",BODY,{"disambiguationData":[OSD([sQuery(id+"F4.wireOp",EDGE,"E27.4.0.1")])]}),"instanceName":"12"});
            var Q112;
            Q112=makeQuery(id+"F6.opPattern","COPY",BODY,{"derivedFrom":makeQuery(id+"F5.opExtrude","SWEPT_BODY",BODY,{"disambiguationData":[OSD([sQuery(id+"F4.wireOp",EDGE,"E27.4.0.0")])]}),"instanceName":"13"});
            var Q113;
            Q113=makeQuery(id+"F6.opPattern","COPY",BODY,{"derivedFrom":makeQuery(id+"F5.opExtrude","SWEPT_BODY",BODY,{"disambiguationData":[OSD([sQuery(id+"F4.wireOp",EDGE,"E27.4.0.1")])]}),"instanceName":"13"});
            var Q114;
            Q114=makeQuery(id+"F6.opPattern","COPY",BODY,{"derivedFrom":makeQuery(id+"F5.opExtrude","SWEPT_BODY",BODY,{"disambiguationData":[OSD([sQuery(id+"F4.wireOp",EDGE,"E27.4.0.0")])]}),"instanceName":"14"});
            var Q115;
            Q115=makeQuery(id+"F6.opPattern","COPY",BODY,{"derivedFrom":makeQuery(id+"F5.opExtrude","SWEPT_BODY",BODY,{"disambiguationData":[OSD([sQuery(id+"F4.wireOp",EDGE,"E27.4.0.1")])]}),"instanceName":"14"});
            var Q116;
            Q116=makeQuery(id+"F6.opPattern","COPY",BODY,{"derivedFrom":makeQuery(id+"F5.opExtrude","SWEPT_BODY",BODY,{"disambiguationData":[OSD([sQuery(id+"F4.wireOp",EDGE,"E27.4.0.0")])]}),"instanceName":"15"});
            var Q117;
            Q117=makeQuery(id+"F6.opPattern","COPY",BODY,{"derivedFrom":makeQuery(id+"F5.opExtrude","SWEPT_BODY",BODY,{"disambiguationData":[OSD([sQuery(id+"F4.wireOp",EDGE,"E27.4.0.1")])]}),"instanceName":"15"});
            var Q118;
            Q118=makeQuery(id+"F5.opExtrude","SWEPT_BODY",BODY,{"disambiguationData":[OSD([sQuery(id+"F4.wireOp",EDGE,"E27.3.0.0")])]});
            var Q119;
            Q119=makeQuery(id+"F5.opExtrude","SWEPT_BODY",BODY,{"disambiguationData":[OSD([sQuery(id+"F4.wireOp",EDGE,"E27.3.0.1")])]});
            var Q120;
            Q120=makeQuery(id+"F6.opPattern","COPY",BODY,{"derivedFrom":makeQuery(id+"F5.opExtrude","SWEPT_BODY",BODY,{"disambiguationData":[OSD([sQuery(id+"F4.wireOp",EDGE,"E27.3.0.0")])]}),"instanceName":"1"});
            var Q121;
            Q121=makeQuery(id+"F6.opPattern","COPY",BODY,{"derivedFrom":makeQuery(id+"F5.opExtrude","SWEPT_BODY",BODY,{"disambiguationData":[OSD([sQuery(id+"F4.wireOp",EDGE,"E27.3.0.1")])]}),"instanceName":"1"});
            var Q122;
            Q122=makeQuery(id+"F6.opPattern","COPY",BODY,{"derivedFrom":makeQuery(id+"F5.opExtrude","SWEPT_BODY",BODY,{"disambiguationData":[OSD([sQuery(id+"F4.wireOp",EDGE,"E27.3.0.0")])]}),"instanceName":"2"});
            var Q123;
            Q123=makeQuery(id+"F6.opPattern","COPY",BODY,{"derivedFrom":makeQuery(id+"F5.opExtrude","SWEPT_BODY",BODY,{"disambiguationData":[OSD([sQuery(id+"F4.wireOp",EDGE,"E27.3.0.1")])]}),"instanceName":"2"});
            var Q124;
            Q124=makeQuery(id+"F6.opPattern","COPY",BODY,{"derivedFrom":makeQuery(id+"F5.opExtrude","SWEPT_BODY",BODY,{"disambiguationData":[OSD([sQuery(id+"F4.wireOp",EDGE,"E27.3.0.0")])]}),"instanceName":"3"});
            var Q125;
            Q125=makeQuery(id+"F6.opPattern","COPY",BODY,{"derivedFrom":makeQuery(id+"F5.opExtrude","SWEPT_BODY",BODY,{"disambiguationData":[OSD([sQuery(id+"F4.wireOp",EDGE,"E27.3.0.1")])]}),"instanceName":"3"});
            var Q126;
            Q126=makeQuery(id+"F6.opPattern","COPY",BODY,{"derivedFrom":makeQuery(id+"F5.opExtrude","SWEPT_BODY",BODY,{"disambiguationData":[OSD([sQuery(id+"F4.wireOp",EDGE,"E27.3.0.0")])]}),"instanceName":"4"});
            var Q127;
            Q127=makeQuery(id+"F6.opPattern","COPY",BODY,{"derivedFrom":makeQuery(id+"F5.opExtrude","SWEPT_BODY",BODY,{"disambiguationData":[OSD([sQuery(id+"F4.wireOp",EDGE,"E27.3.0.1")])]}),"instanceName":"4"});
            var Q128;
            Q128=makeQuery(id+"F6.opPattern","COPY",BODY,{"derivedFrom":makeQuery(id+"F5.opExtrude","SWEPT_BODY",BODY,{"disambiguationData":[OSD([sQuery(id+"F4.wireOp",EDGE,"E27.3.0.0")])]}),"instanceName":"5"});
            var Q129;
            Q129=makeQuery(id+"F6.opPattern","COPY",BODY,{"derivedFrom":makeQuery(id+"F5.opExtrude","SWEPT_BODY",BODY,{"disambiguationData":[OSD([sQuery(id+"F4.wireOp",EDGE,"E27.3.0.1")])]}),"instanceName":"5"});
            var Q130;
            Q130=makeQuery(id+"F6.opPattern","COPY",BODY,{"derivedFrom":makeQuery(id+"F5.opExtrude","SWEPT_BODY",BODY,{"disambiguationData":[OSD([sQuery(id+"F4.wireOp",EDGE,"E27.3.0.0")])]}),"instanceName":"6"});
            var Q131;
            Q131=makeQuery(id+"F6.opPattern","COPY",BODY,{"derivedFrom":makeQuery(id+"F5.opExtrude","SWEPT_BODY",BODY,{"disambiguationData":[OSD([sQuery(id+"F4.wireOp",EDGE,"E27.3.0.0")])]}),"instanceName":"7"});
            var Q132;
            Q132=makeQuery(id+"F6.opPattern","COPY",BODY,{"derivedFrom":makeQuery(id+"F5.opExtrude","SWEPT_BODY",BODY,{"disambiguationData":[OSD([sQuery(id+"F4.wireOp",EDGE,"E27.3.0.1")])]}),"instanceName":"8"});
            var Q133;
            Q133=makeQuery(id+"F6.opPattern","COPY",BODY,{"derivedFrom":makeQuery(id+"F5.opExtrude","SWEPT_BODY",BODY,{"disambiguationData":[OSD([sQuery(id+"F4.wireOp",EDGE,"E27.3.0.0")])]}),"instanceName":"9"});
            var Q134;
            Q134=makeQuery(id+"F6.opPattern","COPY",BODY,{"derivedFrom":makeQuery(id+"F5.opExtrude","SWEPT_BODY",BODY,{"disambiguationData":[OSD([sQuery(id+"F4.wireOp",EDGE,"E27.3.0.1")])]}),"instanceName":"9"});
            var Q135;
            Q135=makeQuery(id+"F6.opPattern","COPY",BODY,{"derivedFrom":makeQuery(id+"F5.opExtrude","SWEPT_BODY",BODY,{"disambiguationData":[OSD([sQuery(id+"F4.wireOp",EDGE,"E27.3.0.0")])]}),"instanceName":"10"});
            var Q136;
            Q136=makeQuery(id+"F6.opPattern","COPY",BODY,{"derivedFrom":makeQuery(id+"F5.opExtrude","SWEPT_BODY",BODY,{"disambiguationData":[OSD([sQuery(id+"F4.wireOp",EDGE,"E27.3.0.1")])]}),"instanceName":"10"});
            var Q137;
            Q137=makeQuery(id+"F6.opPattern","COPY",BODY,{"derivedFrom":makeQuery(id+"F5.opExtrude","SWEPT_BODY",BODY,{"disambiguationData":[OSD([sQuery(id+"F4.wireOp",EDGE,"E27.3.0.0")])]}),"instanceName":"11"});
            var Q138;
            Q138=makeQuery(id+"F6.opPattern","COPY",BODY,{"derivedFrom":makeQuery(id+"F5.opExtrude","SWEPT_BODY",BODY,{"disambiguationData":[OSD([sQuery(id+"F4.wireOp",EDGE,"E27.3.0.1")])]}),"instanceName":"11"});
            var Q139;
            Q139=makeQuery(id+"F6.opPattern","COPY",BODY,{"derivedFrom":makeQuery(id+"F5.opExtrude","SWEPT_BODY",BODY,{"disambiguationData":[OSD([sQuery(id+"F4.wireOp",EDGE,"E27.3.0.0")])]}),"instanceName":"12"});
            var Q140;
            Q140=makeQuery(id+"F6.opPattern","COPY",BODY,{"derivedFrom":makeQuery(id+"F5.opExtrude","SWEPT_BODY",BODY,{"disambiguationData":[OSD([sQuery(id+"F4.wireOp",EDGE,"E27.3.0.1")])]}),"instanceName":"12"});
            var Q141;
            Q141=makeQuery(id+"F6.opPattern","COPY",BODY,{"derivedFrom":makeQuery(id+"F5.opExtrude","SWEPT_BODY",BODY,{"disambiguationData":[OSD([sQuery(id+"F4.wireOp",EDGE,"E27.3.0.0")])]}),"instanceName":"13"});
            var Q142;
            Q142=makeQuery(id+"F6.opPattern","COPY",BODY,{"derivedFrom":makeQuery(id+"F5.opExtrude","SWEPT_BODY",BODY,{"disambiguationData":[OSD([sQuery(id+"F4.wireOp",EDGE,"E27.3.0.1")])]}),"instanceName":"13"});
            var Q143;
            Q143=makeQuery(id+"F6.opPattern","COPY",BODY,{"derivedFrom":makeQuery(id+"F5.opExtrude","SWEPT_BODY",BODY,{"disambiguationData":[OSD([sQuery(id+"F4.wireOp",EDGE,"E27.3.0.0")])]}),"instanceName":"14"});
            var Q144;
            Q144=makeQuery(id+"F6.opPattern","COPY",BODY,{"derivedFrom":makeQuery(id+"F5.opExtrude","SWEPT_BODY",BODY,{"disambiguationData":[OSD([sQuery(id+"F4.wireOp",EDGE,"E27.3.0.1")])]}),"instanceName":"14"});
            var Q145;
            Q145=makeQuery(id+"F6.opPattern","COPY",BODY,{"derivedFrom":makeQuery(id+"F5.opExtrude","SWEPT_BODY",BODY,{"disambiguationData":[OSD([sQuery(id+"F4.wireOp",EDGE,"E27.3.0.0")])]}),"instanceName":"15"});
            var Q146;
            Q146=makeQuery(id+"F6.opPattern","COPY",BODY,{"derivedFrom":makeQuery(id+"F5.opExtrude","SWEPT_BODY",BODY,{"disambiguationData":[OSD([sQuery(id+"F4.wireOp",EDGE,"E27.3.0.1")])]}),"instanceName":"15"});
            var Q147;
            Q147=makeQuery(id+"F5.opExtrude","SWEPT_BODY",BODY,{"disambiguationData":[OSD([sQuery(id+"F4.wireOp",EDGE,"E27.2.0.0")])]});
            var Q148;
            Q148=makeQuery(id+"F5.opExtrude","SWEPT_BODY",BODY,{"disambiguationData":[OSD([sQuery(id+"F4.wireOp",EDGE,"E27.2.0.1")])]});
            var Q149;
            Q149=makeQuery(id+"F6.opPattern","COPY",BODY,{"derivedFrom":makeQuery(id+"F5.opExtrude","SWEPT_BODY",BODY,{"disambiguationData":[OSD([sQuery(id+"F4.wireOp",EDGE,"E27.2.0.0")])]}),"instanceName":"2"});
            var Q150;
            Q150=makeQuery(id+"F6.opPattern","COPY",BODY,{"derivedFrom":makeQuery(id+"F5.opExtrude","SWEPT_BODY",BODY,{"disambiguationData":[OSD([sQuery(id+"F4.wireOp",EDGE,"E27.2.0.1")])]}),"instanceName":"2"});
            var Q151;
            Q151=makeQuery(id+"F6.opPattern","COPY",BODY,{"derivedFrom":makeQuery(id+"F5.opExtrude","SWEPT_BODY",BODY,{"disambiguationData":[OSD([sQuery(id+"F4.wireOp",EDGE,"E27.2.0.0")])]}),"instanceName":"1"});
            var Q152;
            Q152=makeQuery(id+"F6.opPattern","COPY",BODY,{"derivedFrom":makeQuery(id+"F5.opExtrude","SWEPT_BODY",BODY,{"disambiguationData":[OSD([sQuery(id+"F4.wireOp",EDGE,"E27.2.0.1")])]}),"instanceName":"1"});
            var Q153;
            Q153=makeQuery(id+"F6.opPattern","COPY",BODY,{"derivedFrom":makeQuery(id+"F5.opExtrude","SWEPT_BODY",BODY,{"disambiguationData":[OSD([sQuery(id+"F4.wireOp",EDGE,"E27.2.0.0")])]}),"instanceName":"3"});
            var Q154;
            Q154=makeQuery(id+"F6.opPattern","COPY",BODY,{"derivedFrom":makeQuery(id+"F5.opExtrude","SWEPT_BODY",BODY,{"disambiguationData":[OSD([sQuery(id+"F4.wireOp",EDGE,"E27.2.0.1")])]}),"instanceName":"3"});
            var Q155;
            Q155=makeQuery(id+"F6.opPattern","COPY",BODY,{"derivedFrom":makeQuery(id+"F5.opExtrude","SWEPT_BODY",BODY,{"disambiguationData":[OSD([sQuery(id+"F4.wireOp",EDGE,"E27.2.0.0")])]}),"instanceName":"4"});
            var Q156;
            Q156=makeQuery(id+"F6.opPattern","COPY",BODY,{"derivedFrom":makeQuery(id+"F5.opExtrude","SWEPT_BODY",BODY,{"disambiguationData":[OSD([sQuery(id+"F4.wireOp",EDGE,"E27.2.0.1")])]}),"instanceName":"4"});
            var Q157;
            Q157=makeQuery(id+"F6.opPattern","COPY",BODY,{"derivedFrom":makeQuery(id+"F5.opExtrude","SWEPT_BODY",BODY,{"disambiguationData":[OSD([sQuery(id+"F4.wireOp",EDGE,"E27.2.0.0")])]}),"instanceName":"5"});
            var Q158;
            Q158=makeQuery(id+"F6.opPattern","COPY",BODY,{"derivedFrom":makeQuery(id+"F5.opExtrude","SWEPT_BODY",BODY,{"disambiguationData":[OSD([sQuery(id+"F4.wireOp",EDGE,"E27.2.0.1")])]}),"instanceName":"5"});
            var Q159;
            Q159=makeQuery(id+"F6.opPattern","COPY",BODY,{"derivedFrom":makeQuery(id+"F5.opExtrude","SWEPT_BODY",BODY,{"disambiguationData":[OSD([sQuery(id+"F4.wireOp",EDGE,"E27.2.0.0")])]}),"instanceName":"6"});
            var Q160;
            Q160=makeQuery(id+"F6.opPattern","COPY",BODY,{"derivedFrom":makeQuery(id+"F5.opExtrude","SWEPT_BODY",BODY,{"disambiguationData":[OSD([sQuery(id+"F4.wireOp",EDGE,"E27.5.0.1")])]}),"instanceName":"6"});
            var Q161;
            Q161=makeQuery(id+"F6.opPattern","COPY",BODY,{"derivedFrom":makeQuery(id+"F5.opExtrude","SWEPT_BODY",BODY,{"disambiguationData":[OSD([sQuery(id+"F4.wireOp",EDGE,"E27.2.0.0")])]}),"instanceName":"7"});
            var Q162;
            Q162=makeQuery(id+"F6.opPattern","COPY",BODY,{"derivedFrom":makeQuery(id+"F5.opExtrude","SWEPT_BODY",BODY,{"disambiguationData":[OSD([sQuery(id+"F4.wireOp",EDGE,"E27.2.0.1")])]}),"instanceName":"8"});
            var Q163;
            Q163=makeQuery(id+"F6.opPattern","COPY",BODY,{"derivedFrom":makeQuery(id+"F5.opExtrude","SWEPT_BODY",BODY,{"disambiguationData":[OSD([sQuery(id+"F4.wireOp",EDGE,"E27.2.0.0")])]}),"instanceName":"9"});
            var Q164;
            Q164=makeQuery(id+"F6.opPattern","COPY",BODY,{"derivedFrom":makeQuery(id+"F5.opExtrude","SWEPT_BODY",BODY,{"disambiguationData":[OSD([sQuery(id+"F4.wireOp",EDGE,"E27.2.0.1")])]}),"instanceName":"9"});
            var Q165;
            Q165=makeQuery(id+"F6.opPattern","COPY",BODY,{"derivedFrom":makeQuery(id+"F5.opExtrude","SWEPT_BODY",BODY,{"disambiguationData":[OSD([sQuery(id+"F4.wireOp",EDGE,"E27.2.0.0")])]}),"instanceName":"10"});
            var Q166;
            Q166=makeQuery(id+"F6.opPattern","COPY",BODY,{"derivedFrom":makeQuery(id+"F5.opExtrude","SWEPT_BODY",BODY,{"disambiguationData":[OSD([sQuery(id+"F4.wireOp",EDGE,"E27.2.0.1")])]}),"instanceName":"10"});
            var Q167;
            Q167=makeQuery(id+"F6.opPattern","COPY",BODY,{"derivedFrom":makeQuery(id+"F5.opExtrude","SWEPT_BODY",BODY,{"disambiguationData":[OSD([sQuery(id+"F4.wireOp",EDGE,"E27.2.0.0")])]}),"instanceName":"11"});
            var Q168;
            Q168=makeQuery(id+"F6.opPattern","COPY",BODY,{"derivedFrom":makeQuery(id+"F5.opExtrude","SWEPT_BODY",BODY,{"disambiguationData":[OSD([sQuery(id+"F4.wireOp",EDGE,"E27.2.0.1")])]}),"instanceName":"11"});
            var Q169;
            Q169=makeQuery(id+"F6.opPattern","COPY",BODY,{"derivedFrom":makeQuery(id+"F5.opExtrude","SWEPT_BODY",BODY,{"disambiguationData":[OSD([sQuery(id+"F4.wireOp",EDGE,"E27.2.0.0")])]}),"instanceName":"12"});
            var Q170;
            Q170=makeQuery(id+"F6.opPattern","COPY",BODY,{"derivedFrom":makeQuery(id+"F5.opExtrude","SWEPT_BODY",BODY,{"disambiguationData":[OSD([sQuery(id+"F4.wireOp",EDGE,"E27.2.0.1")])]}),"instanceName":"12"});
            var Q171;
            Q171=makeQuery(id+"F6.opPattern","COPY",BODY,{"derivedFrom":makeQuery(id+"F5.opExtrude","SWEPT_BODY",BODY,{"disambiguationData":[OSD([sQuery(id+"F4.wireOp",EDGE,"E27.2.0.0")])]}),"instanceName":"13"});
            var Q172;
            Q172=makeQuery(id+"F6.opPattern","COPY",BODY,{"derivedFrom":makeQuery(id+"F5.opExtrude","SWEPT_BODY",BODY,{"disambiguationData":[OSD([sQuery(id+"F4.wireOp",EDGE,"E27.2.0.1")])]}),"instanceName":"13"});
            var Q173;
            Q173=makeQuery(id+"F6.opPattern","COPY",BODY,{"derivedFrom":makeQuery(id+"F5.opExtrude","SWEPT_BODY",BODY,{"disambiguationData":[OSD([sQuery(id+"F4.wireOp",EDGE,"E27.2.0.0")])]}),"instanceName":"14"});
            var Q174;
            Q174=makeQuery(id+"F6.opPattern","COPY",BODY,{"derivedFrom":makeQuery(id+"F5.opExtrude","SWEPT_BODY",BODY,{"disambiguationData":[OSD([sQuery(id+"F4.wireOp",EDGE,"E27.2.0.1")])]}),"instanceName":"14"});
            var Q175;
            Q175=makeQuery(id+"F6.opPattern","COPY",BODY,{"derivedFrom":makeQuery(id+"F5.opExtrude","SWEPT_BODY",BODY,{"disambiguationData":[OSD([sQuery(id+"F4.wireOp",EDGE,"E27.2.0.0")])]}),"instanceName":"15"});
            var Q176;
            Q176=makeQuery(id+"F6.opPattern","COPY",BODY,{"derivedFrom":makeQuery(id+"F5.opExtrude","SWEPT_BODY",BODY,{"disambiguationData":[OSD([sQuery(id+"F4.wireOp",EDGE,"E27.2.0.1")])]}),"instanceName":"15"});
            var Q177;
            Q177=makeQuery(id+"F5.opExtrude","SWEPT_BODY",BODY,{"disambiguationData":[OSD([sQuery(id+"F4.wireOp",EDGE,"E27.1.0.0")])]});
            var Q178;
            Q178=makeQuery(id+"F5.opExtrude","SWEPT_BODY",BODY,{"disambiguationData":[OSD([sQuery(id+"F4.wireOp",EDGE,"E27.1.0.1")])]});
            var Q179;
            Q179=makeQuery(id+"F6.opPattern","COPY",BODY,{"derivedFrom":makeQuery(id+"F5.opExtrude","SWEPT_BODY",BODY,{"disambiguationData":[OSD([sQuery(id+"F4.wireOp",EDGE,"E27.1.0.0")])]}),"instanceName":"2"});
            var Q180;
            Q180=makeQuery(id+"F6.opPattern","COPY",BODY,{"derivedFrom":makeQuery(id+"F5.opExtrude","SWEPT_BODY",BODY,{"disambiguationData":[OSD([sQuery(id+"F4.wireOp",EDGE,"E27.1.0.1")])]}),"instanceName":"2"});
            var Q181;
            Q181=makeQuery(id+"F6.opPattern","COPY",BODY,{"derivedFrom":makeQuery(id+"F5.opExtrude","SWEPT_BODY",BODY,{"disambiguationData":[OSD([sQuery(id+"F4.wireOp",EDGE,"E27.1.0.0")])]}),"instanceName":"1"});
            var Q182;
            Q182=makeQuery(id+"F6.opPattern","COPY",BODY,{"derivedFrom":makeQuery(id+"F5.opExtrude","SWEPT_BODY",BODY,{"disambiguationData":[OSD([sQuery(id+"F4.wireOp",EDGE,"E27.1.0.1")])]}),"instanceName":"1"});
            var Q183;
            Q183=makeQuery(id+"F6.opPattern","COPY",BODY,{"derivedFrom":makeQuery(id+"F5.opExtrude","SWEPT_BODY",BODY,{"disambiguationData":[OSD([sQuery(id+"F4.wireOp",EDGE,"E27.1.0.0")])]}),"instanceName":"3"});
            var Q184;
            Q184=makeQuery(id+"F6.opPattern","COPY",BODY,{"derivedFrom":makeQuery(id+"F5.opExtrude","SWEPT_BODY",BODY,{"disambiguationData":[OSD([sQuery(id+"F4.wireOp",EDGE,"E27.1.0.1")])]}),"instanceName":"3"});
            var Q185;
            Q185=makeQuery(id+"F6.opPattern","COPY",BODY,{"derivedFrom":makeQuery(id+"F5.opExtrude","SWEPT_BODY",BODY,{"disambiguationData":[OSD([sQuery(id+"F4.wireOp",EDGE,"E27.1.0.0")])]}),"instanceName":"4"});
            var Q186;
            Q186=makeQuery(id+"F6.opPattern","COPY",BODY,{"derivedFrom":makeQuery(id+"F5.opExtrude","SWEPT_BODY",BODY,{"disambiguationData":[OSD([sQuery(id+"F4.wireOp",EDGE,"E27.1.0.1")])]}),"instanceName":"4"});
            var Q187;
            Q187=makeQuery(id+"F6.opPattern","COPY",BODY,{"derivedFrom":makeQuery(id+"F5.opExtrude","SWEPT_BODY",BODY,{"disambiguationData":[OSD([sQuery(id+"F4.wireOp",EDGE,"E27.1.0.0")])]}),"instanceName":"5"});
            var Q188;
            Q188=makeQuery(id+"F6.opPattern","COPY",BODY,{"derivedFrom":makeQuery(id+"F5.opExtrude","SWEPT_BODY",BODY,{"disambiguationData":[OSD([sQuery(id+"F4.wireOp",EDGE,"E27.1.0.1")])]}),"instanceName":"5"});
            var Q189;
            Q189=makeQuery(id+"F6.opPattern","COPY",BODY,{"derivedFrom":makeQuery(id+"F5.opExtrude","SWEPT_BODY",BODY,{"disambiguationData":[OSD([sQuery(id+"F4.wireOp",EDGE,"E27.1.0.0")])]}),"instanceName":"6"});
            var Q190;
            Q190=makeQuery(id+"F6.opPattern","COPY",BODY,{"derivedFrom":makeQuery(id+"F5.opExtrude","SWEPT_BODY",BODY,{"disambiguationData":[OSD([sQuery(id+"F4.wireOp",EDGE,"E27.1.0.0")])]}),"instanceName":"7"});
            var Q191;
            Q191=makeQuery(id+"F6.opPattern","COPY",BODY,{"derivedFrom":makeQuery(id+"F5.opExtrude","SWEPT_BODY",BODY,{"disambiguationData":[OSD([sQuery(id+"F4.wireOp",EDGE,"E27.1.0.1")])]}),"instanceName":"8"});
            var Q192;
            Q192=makeQuery(id+"F6.opPattern","COPY",BODY,{"derivedFrom":makeQuery(id+"F5.opExtrude","SWEPT_BODY",BODY,{"disambiguationData":[OSD([sQuery(id+"F4.wireOp",EDGE,"E27.1.0.0")])]}),"instanceName":"9"});
            var Q193;
            Q193=makeQuery(id+"F6.opPattern","COPY",BODY,{"derivedFrom":makeQuery(id+"F5.opExtrude","SWEPT_BODY",BODY,{"disambiguationData":[OSD([sQuery(id+"F4.wireOp",EDGE,"E27.1.0.1")])]}),"instanceName":"9"});
            var Q194;
            Q194=makeQuery(id+"F6.opPattern","COPY",BODY,{"derivedFrom":makeQuery(id+"F5.opExtrude","SWEPT_BODY",BODY,{"disambiguationData":[OSD([sQuery(id+"F4.wireOp",EDGE,"E27.1.0.0")])]}),"instanceName":"10"});
            var Q195;
            Q195=makeQuery(id+"F6.opPattern","COPY",BODY,{"derivedFrom":makeQuery(id+"F5.opExtrude","SWEPT_BODY",BODY,{"disambiguationData":[OSD([sQuery(id+"F4.wireOp",EDGE,"E27.1.0.1")])]}),"instanceName":"10"});
            var Q196;
            Q196=makeQuery(id+"F6.opPattern","COPY",BODY,{"derivedFrom":makeQuery(id+"F5.opExtrude","SWEPT_BODY",BODY,{"disambiguationData":[OSD([sQuery(id+"F4.wireOp",EDGE,"E27.1.0.0")])]}),"instanceName":"11"});
            var Q197;
            Q197=makeQuery(id+"F6.opPattern","COPY",BODY,{"derivedFrom":makeQuery(id+"F5.opExtrude","SWEPT_BODY",BODY,{"disambiguationData":[OSD([sQuery(id+"F4.wireOp",EDGE,"E27.1.0.1")])]}),"instanceName":"11"});
            var Q198;
            Q198=makeQuery(id+"F6.opPattern","COPY",BODY,{"derivedFrom":makeQuery(id+"F5.opExtrude","SWEPT_BODY",BODY,{"disambiguationData":[OSD([sQuery(id+"F4.wireOp",EDGE,"E27.1.0.0")])]}),"instanceName":"12"});
            var Q199;
            Q199=makeQuery(id+"F6.opPattern","COPY",BODY,{"derivedFrom":makeQuery(id+"F5.opExtrude","SWEPT_BODY",BODY,{"disambiguationData":[OSD([sQuery(id+"F4.wireOp",EDGE,"E27.1.0.1")])]}),"instanceName":"12"});
            var Q200;
            Q200=makeQuery(id+"F6.opPattern","COPY",BODY,{"derivedFrom":makeQuery(id+"F5.opExtrude","SWEPT_BODY",BODY,{"disambiguationData":[OSD([sQuery(id+"F4.wireOp",EDGE,"E27.1.0.0")])]}),"instanceName":"13"});
            var Q201;
            Q201=makeQuery(id+"F6.opPattern","COPY",BODY,{"derivedFrom":makeQuery(id+"F5.opExtrude","SWEPT_BODY",BODY,{"disambiguationData":[OSD([sQuery(id+"F4.wireOp",EDGE,"E27.1.0.1")])]}),"instanceName":"13"});
            var Q202;
            Q202=makeQuery(id+"F6.opPattern","COPY",BODY,{"derivedFrom":makeQuery(id+"F5.opExtrude","SWEPT_BODY",BODY,{"disambiguationData":[OSD([sQuery(id+"F4.wireOp",EDGE,"E27.1.0.0")])]}),"instanceName":"14"});
            var Q203;
            Q203=makeQuery(id+"F6.opPattern","COPY",BODY,{"derivedFrom":makeQuery(id+"F5.opExtrude","SWEPT_BODY",BODY,{"disambiguationData":[OSD([sQuery(id+"F4.wireOp",EDGE,"E27.1.0.1")])]}),"instanceName":"14"});
            var Q204;
            Q204=makeQuery(id+"F6.opPattern","COPY",BODY,{"derivedFrom":makeQuery(id+"F5.opExtrude","SWEPT_BODY",BODY,{"disambiguationData":[OSD([sQuery(id+"F4.wireOp",EDGE,"E27.1.0.0")])]}),"instanceName":"15"});
            var Q205;
            Q205=makeQuery(id+"F6.opPattern","COPY",BODY,{"derivedFrom":makeQuery(id+"F5.opExtrude","SWEPT_BODY",BODY,{"disambiguationData":[OSD([sQuery(id+"F4.wireOp",EDGE,"E27.1.0.1")])]}),"instanceName":"15"});
            var Q206;
            Q206=makeQuery(id+"F5.opExtrude","SWEPT_BODY",BODY,{"disambiguationData":[OSD([sQuery(id+"F4.wireOp",EDGE,"E21")])]});
            var Q207;
            Q207=makeQuery(id+"F5.opExtrude","SWEPT_BODY",BODY,{"disambiguationData":[OSD([sQuery(id+"F4.wireOp",EDGE,"E20")])]});
            var Q208;
            Q208=makeQuery(id+"F6.opPattern","COPY",BODY,{"derivedFrom":makeQuery(id+"F5.opExtrude","SWEPT_BODY",BODY,{"disambiguationData":[OSD([sQuery(id+"F4.wireOp",EDGE,"E20")])]}),"instanceName":"2"});
            var Q209;
            Q209=makeQuery(id+"F6.opPattern","COPY",BODY,{"derivedFrom":makeQuery(id+"F5.opExtrude","SWEPT_BODY",BODY,{"disambiguationData":[OSD([sQuery(id+"F4.wireOp",EDGE,"E21")])]}),"instanceName":"2"});
            var Q210;
            Q210=makeQuery(id+"F6.opPattern","COPY",BODY,{"derivedFrom":makeQuery(id+"F5.opExtrude","SWEPT_BODY",BODY,{"disambiguationData":[OSD([sQuery(id+"F4.wireOp",EDGE,"E21")])]}),"instanceName":"1"});
            var Q211;
            Q211=makeQuery(id+"F6.opPattern","COPY",BODY,{"derivedFrom":makeQuery(id+"F5.opExtrude","SWEPT_BODY",BODY,{"disambiguationData":[OSD([sQuery(id+"F4.wireOp",EDGE,"E20")])]}),"instanceName":"1"});
            var Q212;
            Q212=makeQuery(id+"F6.opPattern","COPY",BODY,{"derivedFrom":makeQuery(id+"F5.opExtrude","SWEPT_BODY",BODY,{"disambiguationData":[OSD([sQuery(id+"F4.wireOp",EDGE,"E20")])]}),"instanceName":"3"});
            var Q213;
            Q213=makeQuery(id+"F6.opPattern","COPY",BODY,{"derivedFrom":makeQuery(id+"F5.opExtrude","SWEPT_BODY",BODY,{"disambiguationData":[OSD([sQuery(id+"F4.wireOp",EDGE,"E21")])]}),"instanceName":"3"});
            var Q214;
            Q214=makeQuery(id+"F6.opPattern","COPY",BODY,{"derivedFrom":makeQuery(id+"F5.opExtrude","SWEPT_BODY",BODY,{"disambiguationData":[OSD([sQuery(id+"F4.wireOp",EDGE,"E20")])]}),"instanceName":"4"});
            var Q215;
            Q215=makeQuery(id+"F6.opPattern","COPY",BODY,{"derivedFrom":makeQuery(id+"F5.opExtrude","SWEPT_BODY",BODY,{"disambiguationData":[OSD([sQuery(id+"F4.wireOp",EDGE,"E21")])]}),"instanceName":"4"});
            var Q216;
            Q216=makeQuery(id+"F6.opPattern","COPY",BODY,{"derivedFrom":makeQuery(id+"F5.opExtrude","SWEPT_BODY",BODY,{"disambiguationData":[OSD([sQuery(id+"F4.wireOp",EDGE,"E20")])]}),"instanceName":"5"});
            var Q217;
            Q217=makeQuery(id+"F6.opPattern","COPY",BODY,{"derivedFrom":makeQuery(id+"F5.opExtrude","SWEPT_BODY",BODY,{"disambiguationData":[OSD([sQuery(id+"F4.wireOp",EDGE,"E21")])]}),"instanceName":"5"});
            var Q218;
            Q218=makeQuery(id+"F6.opPattern","COPY",BODY,{"derivedFrom":makeQuery(id+"F5.opExtrude","SWEPT_BODY",BODY,{"disambiguationData":[OSD([sQuery(id+"F4.wireOp",EDGE,"E21")])]}),"instanceName":"6"});
            var Q219;
            Q219=makeQuery(id+"F6.opPattern","COPY",BODY,{"derivedFrom":makeQuery(id+"F5.opExtrude","SWEPT_BODY",BODY,{"disambiguationData":[OSD([sQuery(id+"F4.wireOp",EDGE,"E21")])]}),"instanceName":"7"});
            var Q220;
            Q220=makeQuery(id+"F6.opPattern","COPY",BODY,{"derivedFrom":makeQuery(id+"F5.opExtrude","SWEPT_BODY",BODY,{"disambiguationData":[OSD([sQuery(id+"F4.wireOp",EDGE,"E20")])]}),"instanceName":"8"});
            var Q221;
            Q221=makeQuery(id+"F6.opPattern","COPY",BODY,{"derivedFrom":makeQuery(id+"F5.opExtrude","SWEPT_BODY",BODY,{"disambiguationData":[OSD([sQuery(id+"F4.wireOp",EDGE,"E20")])]}),"instanceName":"9"});
            var Q222;
            Q222=makeQuery(id+"F6.opPattern","COPY",BODY,{"derivedFrom":makeQuery(id+"F5.opExtrude","SWEPT_BODY",BODY,{"disambiguationData":[OSD([sQuery(id+"F4.wireOp",EDGE,"E21")])]}),"instanceName":"9"});
            var Q223;
            Q223=makeQuery(id+"F6.opPattern","COPY",BODY,{"derivedFrom":makeQuery(id+"F5.opExtrude","SWEPT_BODY",BODY,{"disambiguationData":[OSD([sQuery(id+"F4.wireOp",EDGE,"E20")])]}),"instanceName":"10"});
            var Q224;
            Q224=makeQuery(id+"F6.opPattern","COPY",BODY,{"derivedFrom":makeQuery(id+"F5.opExtrude","SWEPT_BODY",BODY,{"disambiguationData":[OSD([sQuery(id+"F4.wireOp",EDGE,"E21")])]}),"instanceName":"10"});
            var Q225;
            Q225=makeQuery(id+"F6.opPattern","COPY",BODY,{"derivedFrom":makeQuery(id+"F5.opExtrude","SWEPT_BODY",BODY,{"disambiguationData":[OSD([sQuery(id+"F4.wireOp",EDGE,"E20")])]}),"instanceName":"11"});
            var Q226;
            Q226=makeQuery(id+"F6.opPattern","COPY",BODY,{"derivedFrom":makeQuery(id+"F5.opExtrude","SWEPT_BODY",BODY,{"disambiguationData":[OSD([sQuery(id+"F4.wireOp",EDGE,"E21")])]}),"instanceName":"11"});
            var Q227;
            Q227=makeQuery(id+"F6.opPattern","COPY",BODY,{"derivedFrom":makeQuery(id+"F5.opExtrude","SWEPT_BODY",BODY,{"disambiguationData":[OSD([sQuery(id+"F4.wireOp",EDGE,"E20")])]}),"instanceName":"12"});
            var Q228;
            Q228=makeQuery(id+"F6.opPattern","COPY",BODY,{"derivedFrom":makeQuery(id+"F5.opExtrude","SWEPT_BODY",BODY,{"disambiguationData":[OSD([sQuery(id+"F4.wireOp",EDGE,"E21")])]}),"instanceName":"12"});
            var Q229;
            Q229=makeQuery(id+"F6.opPattern","COPY",BODY,{"derivedFrom":makeQuery(id+"F5.opExtrude","SWEPT_BODY",BODY,{"disambiguationData":[OSD([sQuery(id+"F4.wireOp",EDGE,"E20")])]}),"instanceName":"13"});
            var Q230;
            Q230=makeQuery(id+"F6.opPattern","COPY",BODY,{"derivedFrom":makeQuery(id+"F5.opExtrude","SWEPT_BODY",BODY,{"disambiguationData":[OSD([sQuery(id+"F4.wireOp",EDGE,"E21")])]}),"instanceName":"13"});
            var Q231;
            Q231=makeQuery(id+"F6.opPattern","COPY",BODY,{"derivedFrom":makeQuery(id+"F5.opExtrude","SWEPT_BODY",BODY,{"disambiguationData":[OSD([sQuery(id+"F4.wireOp",EDGE,"E20")])]}),"instanceName":"14"});
            var Q232;
            Q232=makeQuery(id+"F6.opPattern","COPY",BODY,{"derivedFrom":makeQuery(id+"F5.opExtrude","SWEPT_BODY",BODY,{"disambiguationData":[OSD([sQuery(id+"F4.wireOp",EDGE,"E21")])]}),"instanceName":"14"});
            var Q233;
            Q233=makeQuery(id+"F6.opPattern","COPY",BODY,{"derivedFrom":makeQuery(id+"F5.opExtrude","SWEPT_BODY",BODY,{"disambiguationData":[OSD([sQuery(id+"F4.wireOp",EDGE,"E20")])]}),"instanceName":"15"});
            var Q234;
            Q234=makeQuery(id+"F6.opPattern","COPY",BODY,{"derivedFrom":makeQuery(id+"F5.opExtrude","SWEPT_BODY",BODY,{"disambiguationData":[OSD([sQuery(id+"F4.wireOp",EDGE,"E21")])]}),"instanceName":"15"});
            var Q235;
            Q235=makeQuery(id+"F6.opPattern","COPY",BODY,{"derivedFrom":makeQuery(id+"F5.opExtrude","SWEPT_BODY",BODY,{"disambiguationData":[OSD([sQuery(id+"F4.wireOp",EDGE,"E27.4.0.1")])]}),"instanceName":"6"});
            var Q236;
            Q236=makeQuery(id+"F6.opPattern","COPY",BODY,{"derivedFrom":makeQuery(id+"F5.opExtrude","SWEPT_BODY",BODY,{"disambiguationData":[OSD([sQuery(id+"F4.wireOp",EDGE,"E27.3.0.1")])]}),"instanceName":"6"});
            var Q237;
            Q237=makeQuery(id+"F6.opPattern","COPY",BODY,{"derivedFrom":makeQuery(id+"F5.opExtrude","SWEPT_BODY",BODY,{"disambiguationData":[OSD([sQuery(id+"F4.wireOp",EDGE,"E27.2.0.1")])]}),"instanceName":"6"});
            var Q238;
            Q238=makeQuery(id+"F6.opPattern","COPY",BODY,{"derivedFrom":makeQuery(id+"F5.opExtrude","SWEPT_BODY",BODY,{"disambiguationData":[OSD([sQuery(id+"F4.wireOp",EDGE,"E27.1.0.1")])]}),"instanceName":"6"});
            var Q239;
            Q239=makeQuery(id+"F6.opPattern","COPY",BODY,{"derivedFrom":makeQuery(id+"F5.opExtrude","SWEPT_BODY",BODY,{"disambiguationData":[OSD([sQuery(id+"F4.wireOp",EDGE,"E20")])]}),"instanceName":"6"});
            var Q240;
            Q240=makeQuery(id+"F6.opPattern","COPY",BODY,{"derivedFrom":makeQuery(id+"F5.opExtrude","SWEPT_BODY",BODY,{"disambiguationData":[OSD([sQuery(id+"F4.wireOp",EDGE,"E27.7.0.1")])]}),"instanceName":"7"});
            var Q241;
            Q241=makeQuery(id+"F6.opPattern","COPY",BODY,{"derivedFrom":makeQuery(id+"F5.opExtrude","SWEPT_BODY",BODY,{"disambiguationData":[OSD([sQuery(id+"F4.wireOp",EDGE,"E27.7.0.0")])]}),"instanceName":"8"});
            var Q242;
            Q242=makeQuery(id+"F6.opPattern","COPY",BODY,{"derivedFrom":makeQuery(id+"F5.opExtrude","SWEPT_BODY",BODY,{"disambiguationData":[OSD([sQuery(id+"F4.wireOp",EDGE,"E27.6.0.1")])]}),"instanceName":"7"});
            var Q243;
            Q243=makeQuery(id+"F6.opPattern","COPY",BODY,{"derivedFrom":makeQuery(id+"F5.opExtrude","SWEPT_BODY",BODY,{"disambiguationData":[OSD([sQuery(id+"F4.wireOp",EDGE,"E27.6.0.0")])]}),"instanceName":"8"});
            var Q244;
            Q244=makeQuery(id+"F6.opPattern","COPY",BODY,{"derivedFrom":makeQuery(id+"F5.opExtrude","SWEPT_BODY",BODY,{"disambiguationData":[OSD([sQuery(id+"F4.wireOp",EDGE,"E27.5.0.1")])]}),"instanceName":"7"});
            var Q245;
            Q245=makeQuery(id+"F6.opPattern","COPY",BODY,{"derivedFrom":makeQuery(id+"F5.opExtrude","SWEPT_BODY",BODY,{"disambiguationData":[OSD([sQuery(id+"F4.wireOp",EDGE,"E27.5.0.0")])]}),"instanceName":"8"});
            var Q246;
            Q246=makeQuery(id+"F6.opPattern","COPY",BODY,{"derivedFrom":makeQuery(id+"F5.opExtrude","SWEPT_BODY",BODY,{"disambiguationData":[OSD([sQuery(id+"F4.wireOp",EDGE,"E27.4.0.1")])]}),"instanceName":"7"});
            var Q247;
            Q247=makeQuery(id+"F6.opPattern","COPY",BODY,{"derivedFrom":makeQuery(id+"F5.opExtrude","SWEPT_BODY",BODY,{"disambiguationData":[OSD([sQuery(id+"F4.wireOp",EDGE,"E27.4.0.0")])]}),"instanceName":"8"});
            var Q248;
            Q248=makeQuery(id+"F6.opPattern","COPY",BODY,{"derivedFrom":makeQuery(id+"F5.opExtrude","SWEPT_BODY",BODY,{"disambiguationData":[OSD([sQuery(id+"F4.wireOp",EDGE,"E27.3.0.1")])]}),"instanceName":"7"});
            var Q249;
            Q249=makeQuery(id+"F6.opPattern","COPY",BODY,{"derivedFrom":makeQuery(id+"F5.opExtrude","SWEPT_BODY",BODY,{"disambiguationData":[OSD([sQuery(id+"F4.wireOp",EDGE,"E27.3.0.0")])]}),"instanceName":"8"});
            var Q250;
            Q250=makeQuery(id+"F6.opPattern","COPY",BODY,{"derivedFrom":makeQuery(id+"F5.opExtrude","SWEPT_BODY",BODY,{"disambiguationData":[OSD([sQuery(id+"F4.wireOp",EDGE,"E27.2.0.1")])]}),"instanceName":"7"});
            var Q251;
            Q251=makeQuery(id+"F6.opPattern","COPY",BODY,{"derivedFrom":makeQuery(id+"F5.opExtrude","SWEPT_BODY",BODY,{"disambiguationData":[OSD([sQuery(id+"F4.wireOp",EDGE,"E27.2.0.0")])]}),"instanceName":"8"});
            var Q252;
            Q252=makeQuery(id+"F6.opPattern","COPY",BODY,{"derivedFrom":makeQuery(id+"F5.opExtrude","SWEPT_BODY",BODY,{"disambiguationData":[OSD([sQuery(id+"F4.wireOp",EDGE,"E27.1.0.1")])]}),"instanceName":"7"});
            var Q253;
            Q253=makeQuery(id+"F6.opPattern","COPY",BODY,{"derivedFrom":makeQuery(id+"F5.opExtrude","SWEPT_BODY",BODY,{"disambiguationData":[OSD([sQuery(id+"F4.wireOp",EDGE,"E27.1.0.0")])]}),"instanceName":"8"});
            var Q254;
            Q254=makeQuery(id+"F6.opPattern","COPY",BODY,{"derivedFrom":makeQuery(id+"F5.opExtrude","SWEPT_BODY",BODY,{"disambiguationData":[OSD([sQuery(id+"F4.wireOp",EDGE,"E20")])]}),"instanceName":"7"});
            var Q255;
            Q255=makeQuery(id+"F6.opPattern","COPY",BODY,{"derivedFrom":makeQuery(id+"F5.opExtrude","SWEPT_BODY",BODY,{"disambiguationData":[OSD([sQuery(id+"F4.wireOp",EDGE,"E21")])]}),"instanceName":"8"});
            var Q256;
            Q256=makeQuery(id+"F3.opPattern","COPY",BODY,{"derivedFrom":makeQuery(id+"F1.opExtrude","SWEPT_BODY",BODY,{"disambiguationData":[OSD([sQuery(id+"F0.wireOp",EDGE,"E5"),sQuery(id+"F0.wireOp",EDGE,"E6"),sQuery(id+"F0.wireOp",EDGE,"E7"),sQuery(id+"F0.wireOp",EDGE,"E8")])]}),"instanceName":"11"});
            var Q257;
            Q257=makeQuery(id+"F3.opPattern","COPY",BODY,{"derivedFrom":makeQuery(id+"F1.opExtrude","SWEPT_BODY",BODY,{"disambiguationData":[OSD([sQuery(id+"F0.wireOp",EDGE,"E5"),sQuery(id+"F0.wireOp",EDGE,"E6"),sQuery(id+"F0.wireOp",EDGE,"E7"),sQuery(id+"F0.wireOp",EDGE,"E8")])]}),"instanceName":"10"});
            var Q258;
            Q258=makeQuery(id+"F3.opPattern","COPY",BODY,{"derivedFrom":makeQuery(id+"F1.opExtrude","SWEPT_BODY",BODY,{"disambiguationData":[OSD([sQuery(id+"F0.wireOp",EDGE,"E5"),sQuery(id+"F0.wireOp",EDGE,"E6"),sQuery(id+"F0.wireOp",EDGE,"E7"),sQuery(id+"F0.wireOp",EDGE,"E8")])]}),"instanceName":"9"});
            var Q259;
            Q259=makeQuery(id+"F3.opPattern","COPY",BODY,{"derivedFrom":makeQuery(id+"F1.opExtrude","SWEPT_BODY",BODY,{"disambiguationData":[OSD([sQuery(id+"F0.wireOp",EDGE,"E5"),sQuery(id+"F0.wireOp",EDGE,"E6"),sQuery(id+"F0.wireOp",EDGE,"E7"),sQuery(id+"F0.wireOp",EDGE,"E8")])]}),"instanceName":"8"});
            var Q260;
            Q260=makeQuery(id+"F3.opPattern","COPY",BODY,{"derivedFrom":makeQuery(id+"F1.opExtrude","SWEPT_BODY",BODY,{"disambiguationData":[OSD([sQuery(id+"F0.wireOp",EDGE,"E5"),sQuery(id+"F0.wireOp",EDGE,"E6"),sQuery(id+"F0.wireOp",EDGE,"E7"),sQuery(id+"F0.wireOp",EDGE,"E8")])]}),"instanceName":"7"});
            var Q261;
            Q261=makeQuery(id+"F3.opPattern","COPY",BODY,{"derivedFrom":makeQuery(id+"F1.opExtrude","SWEPT_BODY",BODY,{"disambiguationData":[OSD([sQuery(id+"F0.wireOp",EDGE,"E5"),sQuery(id+"F0.wireOp",EDGE,"E6"),sQuery(id+"F0.wireOp",EDGE,"E7"),sQuery(id+"F0.wireOp",EDGE,"E8")])]}),"instanceName":"6"});
            var Q262;
            Q262=makeQuery(id+"F3.opPattern","COPY",BODY,{"derivedFrom":makeQuery(id+"F1.opExtrude","SWEPT_BODY",BODY,{"disambiguationData":[OSD([sQuery(id+"F0.wireOp",EDGE,"E5"),sQuery(id+"F0.wireOp",EDGE,"E6"),sQuery(id+"F0.wireOp",EDGE,"E7"),sQuery(id+"F0.wireOp",EDGE,"E8")])]}),"instanceName":"5"});
            var Q263;
            Q263=makeQuery(id+"F3.opPattern","COPY",BODY,{"derivedFrom":makeQuery(id+"F1.opExtrude","SWEPT_BODY",BODY,{"disambiguationData":[OSD([sQuery(id+"F0.wireOp",EDGE,"E5"),sQuery(id+"F0.wireOp",EDGE,"E6"),sQuery(id+"F0.wireOp",EDGE,"E7"),sQuery(id+"F0.wireOp",EDGE,"E8")])]}),"instanceName":"4"});
            var Q264;
            Q264=makeQuery(id+"F3.opPattern","COPY",BODY,{"derivedFrom":makeQuery(id+"F1.opExtrude","SWEPT_BODY",BODY,{"disambiguationData":[OSD([sQuery(id+"F0.wireOp",EDGE,"E5"),sQuery(id+"F0.wireOp",EDGE,"E6"),sQuery(id+"F0.wireOp",EDGE,"E7"),sQuery(id+"F0.wireOp",EDGE,"E8")])]}),"instanceName":"3"});
            var Q265;
            Q265=makeQuery(id+"F3.opPattern","COPY",BODY,{"derivedFrom":makeQuery(id+"F1.opExtrude","SWEPT_BODY",BODY,{"disambiguationData":[OSD([sQuery(id+"F0.wireOp",EDGE,"E5"),sQuery(id+"F0.wireOp",EDGE,"E6"),sQuery(id+"F0.wireOp",EDGE,"E7"),sQuery(id+"F0.wireOp",EDGE,"E8")])]}),"instanceName":"2"});
            var Q266;
            Q266=makeQuery(id+"F3.opPattern","COPY",BODY,{"derivedFrom":makeQuery(id+"F1.opExtrude","SWEPT_BODY",BODY,{"disambiguationData":[OSD([sQuery(id+"F0.wireOp",EDGE,"E5"),sQuery(id+"F0.wireOp",EDGE,"E6"),sQuery(id+"F0.wireOp",EDGE,"E7"),sQuery(id+"F0.wireOp",EDGE,"E8")])]}),"instanceName":"1"});
            var Q267;
            Q267=makeQuery(id+"F1.opExtrude","SWEPT_BODY",BODY,{"disambiguationData":[OSD([sQuery(id+"F0.wireOp",EDGE,"E5"),sQuery(id+"F0.wireOp",EDGE,"E6"),sQuery(id+"F0.wireOp",EDGE,"E7"),sQuery(id+"F0.wireOp",EDGE,"E8")])]});
            var Q268;
            Q268=makeQuery(id+"F3.opPattern","COPY",BODY,{"derivedFrom":makeQuery(id+"F1.opExtrude","SWEPT_BODY",BODY,{"disambiguationData":[OSD([sQuery(id+"F0.wireOp",EDGE,"E5"),sQuery(id+"F0.wireOp",EDGE,"E6"),sQuery(id+"F0.wireOp",EDGE,"E7"),sQuery(id+"F0.wireOp",EDGE,"E8")])]}),"instanceName":"15"});
            var Q269;
            Q269=makeQuery(id+"F3.opPattern","COPY",BODY,{"derivedFrom":makeQuery(id+"F1.opExtrude","SWEPT_BODY",BODY,{"disambiguationData":[OSD([sQuery(id+"F0.wireOp",EDGE,"E5"),sQuery(id+"F0.wireOp",EDGE,"E6"),sQuery(id+"F0.wireOp",EDGE,"E7"),sQuery(id+"F0.wireOp",EDGE,"E8")])]}),"instanceName":"14"});
            var Q270;
            Q270=makeQuery(id+"F3.opPattern","COPY",BODY,{"derivedFrom":makeQuery(id+"F1.opExtrude","SWEPT_BODY",BODY,{"disambiguationData":[OSD([sQuery(id+"F0.wireOp",EDGE,"E5"),sQuery(id+"F0.wireOp",EDGE,"E6"),sQuery(id+"F0.wireOp",EDGE,"E7"),sQuery(id+"F0.wireOp",EDGE,"E8")])]}),"instanceName":"13"});
            var Q271;
            Q271=makeQuery(id+"F3.opPattern","COPY",BODY,{"derivedFrom":makeQuery(id+"F1.opExtrude","SWEPT_BODY",BODY,{"disambiguationData":[OSD([sQuery(id+"F0.wireOp",EDGE,"E5"),sQuery(id+"F0.wireOp",EDGE,"E6"),sQuery(id+"F0.wireOp",EDGE,"E7"),sQuery(id+"F0.wireOp",EDGE,"E8")])]}),"instanceName":"12"});
            booleanBodies(context, id + "F7", {"operationType" : BooleanOperationType.SUBTRACTION, "tools" : qUnion([Q0, Q1, Q2, Q3, Q4, Q5, Q6, Q7, Q8, Q9, Q10, Q11, Q12, Q13, Q14, Q15, Q16, Q17, Q18, Q19, Q20, Q21, Q22, Q23, Q24, Q25, Q26, Q27, Q28, Q29, Q30, Q31, Q32, Q33, Q34, Q35, Q36, Q37, Q38, Q39, Q40, Q41, Q42, Q43, Q44, Q45, Q46, Q47, Q48, Q49, Q50, Q51, Q52, Q53, Q54, Q55, Q56, Q57, Q58, Q59, Q60, Q61, Q62, Q63, Q64, Q65, Q66, Q67, Q68, Q69, Q70, Q71, Q72, Q73, Q74, Q75, Q76, Q77, Q78, Q79, Q80, Q81, Q82, Q83, Q84, Q85, Q86, Q87, Q88, Q89, Q90, Q91, Q92, Q93, Q94, Q95, Q96, Q97, Q98, Q99, Q100, Q101, Q102, Q103, Q104, Q105, Q106, Q107, Q108, Q109, Q110, Q111, Q112, Q113, Q114, Q115, Q116, Q117, Q118, Q119, Q120, Q121, Q122, Q123, Q124, Q125, Q126, Q127, Q128, Q129, Q130, Q131, Q132, Q133, Q134, Q135, Q136, Q137, Q138, Q139, Q140, Q141, Q142, Q143, Q144, Q145, Q146, Q147, Q148, Q149, Q150, Q151, Q152, Q153, Q154, Q155, Q156, Q157, Q158, Q159, Q160, Q161, Q162, Q163, Q164, Q165, Q166, Q167, Q168, Q169, Q170, Q171, Q172, Q173, Q174, Q175, Q176, Q177, Q178, Q179, Q180, Q181, Q182, Q183, Q184, Q185, Q186, Q187, Q188, Q189, Q190, Q191, Q192, Q193, Q194, Q195, Q196, Q197, Q198, Q199, Q200, Q201, Q202, Q203, Q204, Q205, Q206, Q207, Q208, Q209, Q210, Q211, Q212, Q213, Q214, Q215, Q216, Q217, Q218, Q219, Q220, Q221, Q222, Q223, Q224, Q225, Q226, Q227, Q228, Q229, Q230, Q231, Q232, Q233, Q234, Q235, Q236, Q237, Q238, Q239, Q240, Q241, Q242, Q243, Q244, Q245, Q246, Q247, Q248, Q249, Q250, Q251, Q252, Q253, Q254, Q255]), "targets" : qUnion([Q256, Q257, Q258, Q259, Q260, Q261, Q262, Q263, Q264, Q265, Q266, Q267, Q268, Q269, Q270, Q271])});
        }
        {
            var Q0;
            Q0=makeQuery(id+"F3.opPattern","COPY",FACE,{"derivedFrom":makeQuery(id+"F1.opExtrude","SWEPT_FACE",FACE,{"disambiguationData":[OSD([sQuery(id+"F0.wireOp",EDGE,"E5")])]}),"instanceName":"5"});
            var sketch = newSketch(context, id + "F8", { "sketchPlane" : qUnion([Q0])});
            skLineSegment(sketch, "E28", {"start": v(146.05, 0) * mm, "end": v(-146.05, 0) * mm, "construction": true});
            skCircle(sketch, "E29", {"center": v(0, 0) * mm, "radius": 1.59 * mm});
            skCircle(sketch, "E30", {"center": v(133.49, 0) * mm, "radius": 1.59 * mm});
            skCircle(sketch, "E31", {"center": v(-133, 0) * mm, "radius": 1.59 * mm});
            skSolve(sketch);
        }
        {
            var Q0;
            Q0=makeQuery(id+"F8.imprint","IMPRINT",FACE,{"disambiguationData":[TD([[makeQuery(id+"F8.imprint","IMPRINT",EDGE,{"derivedFrom":sQuery(id+"F8.wireOp",EDGE,"E31")}),1.0]])]});
            var Q1;
            Q1=makeQuery(id+"F8.imprint","IMPRINT",FACE,{"disambiguationData":[TD([[makeQuery(id+"F8.imprint","IMPRINT",EDGE,{"derivedFrom":sQuery(id+"F8.wireOp",EDGE,"E29")}),1.0]])]});
            var Q2;
            Q2=makeQuery(id+"F8.imprint","IMPRINT",FACE,{"disambiguationData":[TD([[makeQuery(id+"F8.imprint","IMPRINT",EDGE,{"derivedFrom":sQuery(id+"F8.wireOp",EDGE,"E30")}),1.0]])]});
            extrude(context, id + "F9", {"entities" : qUnion([Q0, Q1, Q2]), "oppositeDirection" : true, "depth" : 25.4 * mm});
        }
        {
            var Q0;
            Q0=makeQuery(id+"F9.opExtrude","SWEPT_BODY",BODY,{"disambiguationData":[OSD([sQuery(id+"F8.wireOp",EDGE,"E31")])]});
            var Q1;
            Q1=makeQuery(id+"F9.opExtrude","SWEPT_BODY",BODY,{"disambiguationData":[OSD([sQuery(id+"F8.wireOp",EDGE,"E29")])]});
            var Q2;
            Q2=makeQuery(id+"F9.opExtrude","SWEPT_BODY",BODY,{"disambiguationData":[OSD([sQuery(id+"F8.wireOp",EDGE,"E30")])]});
            var Q3;
            Q3=sQuery(id+"F2.wireOp",EDGE,"E9");
            circularPattern(context, id + "F10", {"entities" : qUnion([Q0, Q1, Q2]), "axis" : qUnion([Q3]), "angle" : 360 * degree, "instanceCount" : 16, "equalSpace" : true});
        }
        {
            var Q0;
            Q0=makeQuery(id+"F10.opPattern","COPY",BODY,{"derivedFrom":makeQuery(id+"F9.opExtrude","SWEPT_BODY",BODY,{"disambiguationData":[OSD([sQuery(id+"F8.wireOp",EDGE,"E31")])]}),"instanceName":"1"});
            var Q1;
            Q1=makeQuery(id+"F10.opPattern","COPY",BODY,{"derivedFrom":makeQuery(id+"F9.opExtrude","SWEPT_BODY",BODY,{"disambiguationData":[OSD([sQuery(id+"F8.wireOp",EDGE,"E31")])]}),"instanceName":"2"});
            var Q2;
            Q2=makeQuery(id+"F10.opPattern","COPY",BODY,{"derivedFrom":makeQuery(id+"F9.opExtrude","SWEPT_BODY",BODY,{"disambiguationData":[OSD([sQuery(id+"F8.wireOp",EDGE,"E31")])]}),"instanceName":"5"});
            var Q3;
            Q3=makeQuery(id+"F10.opPattern","COPY",BODY,{"derivedFrom":makeQuery(id+"F9.opExtrude","SWEPT_BODY",BODY,{"disambiguationData":[OSD([sQuery(id+"F8.wireOp",EDGE,"E31")])]}),"instanceName":"14"});
            var Q4;
            Q4=makeQuery(id+"F10.opPattern","COPY",BODY,{"derivedFrom":makeQuery(id+"F9.opExtrude","SWEPT_BODY",BODY,{"disambiguationData":[OSD([sQuery(id+"F8.wireOp",EDGE,"E29")])]}),"instanceName":"1"});
            var Q5;
            Q5=makeQuery(id+"F10.opPattern","COPY",BODY,{"derivedFrom":makeQuery(id+"F9.opExtrude","SWEPT_BODY",BODY,{"disambiguationData":[OSD([sQuery(id+"F8.wireOp",EDGE,"E29")])]}),"instanceName":"2"});
            var Q6;
            Q6=makeQuery(id+"F10.opPattern","COPY",BODY,{"derivedFrom":makeQuery(id+"F9.opExtrude","SWEPT_BODY",BODY,{"disambiguationData":[OSD([sQuery(id+"F8.wireOp",EDGE,"E29")])]}),"instanceName":"5"});
            var Q7;
            Q7=makeQuery(id+"F10.opPattern","COPY",BODY,{"derivedFrom":makeQuery(id+"F9.opExtrude","SWEPT_BODY",BODY,{"disambiguationData":[OSD([sQuery(id+"F8.wireOp",EDGE,"E29")])]}),"instanceName":"14"});
            var Q8;
            Q8=makeQuery(id+"F10.opPattern","COPY",BODY,{"derivedFrom":makeQuery(id+"F9.opExtrude","SWEPT_BODY",BODY,{"disambiguationData":[OSD([sQuery(id+"F8.wireOp",EDGE,"E30")])]}),"instanceName":"1"});
            var Q9;
            Q9=makeQuery(id+"F10.opPattern","COPY",BODY,{"derivedFrom":makeQuery(id+"F9.opExtrude","SWEPT_BODY",BODY,{"disambiguationData":[OSD([sQuery(id+"F8.wireOp",EDGE,"E30")])]}),"instanceName":"2"});
            var Q10;
            Q10=makeQuery(id+"F10.opPattern","COPY",BODY,{"derivedFrom":makeQuery(id+"F9.opExtrude","SWEPT_BODY",BODY,{"disambiguationData":[OSD([sQuery(id+"F8.wireOp",EDGE,"E30")])]}),"instanceName":"5"});
            var Q11;
            Q11=makeQuery(id+"F10.opPattern","COPY",BODY,{"derivedFrom":makeQuery(id+"F9.opExtrude","SWEPT_BODY",BODY,{"disambiguationData":[OSD([sQuery(id+"F8.wireOp",EDGE,"E30")])]}),"instanceName":"14"});
            var Q12;
            Q12=makeQuery(id+"F9.opExtrude","SWEPT_BODY",BODY,{"disambiguationData":[OSD([sQuery(id+"F8.wireOp",EDGE,"E31")])]});
            var Q13;
            Q13=makeQuery(id+"F10.opPattern","COPY",BODY,{"derivedFrom":makeQuery(id+"F9.opExtrude","SWEPT_BODY",BODY,{"disambiguationData":[OSD([sQuery(id+"F8.wireOp",EDGE,"E31")])]}),"instanceName":"15"});
            var Q14;
            Q14=makeQuery(id+"F9.opExtrude","SWEPT_BODY",BODY,{"disambiguationData":[OSD([sQuery(id+"F8.wireOp",EDGE,"E29")])]});
            var Q15;
            Q15=makeQuery(id+"F10.opPattern","COPY",BODY,{"derivedFrom":makeQuery(id+"F9.opExtrude","SWEPT_BODY",BODY,{"disambiguationData":[OSD([sQuery(id+"F8.wireOp",EDGE,"E29")])]}),"instanceName":"15"});
            var Q16;
            Q16=makeQuery(id+"F9.opExtrude","SWEPT_BODY",BODY,{"disambiguationData":[OSD([sQuery(id+"F8.wireOp",EDGE,"E30")])]});
            var Q17;
            Q17=makeQuery(id+"F10.opPattern","COPY",BODY,{"derivedFrom":makeQuery(id+"F9.opExtrude","SWEPT_BODY",BODY,{"disambiguationData":[OSD([sQuery(id+"F8.wireOp",EDGE,"E30")])]}),"instanceName":"15"});
            var Q18;
            Q18=makeQuery(id+"F10.opPattern","COPY",BODY,{"derivedFrom":makeQuery(id+"F9.opExtrude","SWEPT_BODY",BODY,{"disambiguationData":[OSD([sQuery(id+"F8.wireOp",EDGE,"E31")])]}),"instanceName":"3"});
            var Q19;
            Q19=makeQuery(id+"F10.opPattern","COPY",BODY,{"derivedFrom":makeQuery(id+"F9.opExtrude","SWEPT_BODY",BODY,{"disambiguationData":[OSD([sQuery(id+"F8.wireOp",EDGE,"E31")])]}),"instanceName":"4"});
            var Q20;
            Q20=makeQuery(id+"F10.opPattern","COPY",BODY,{"derivedFrom":makeQuery(id+"F9.opExtrude","SWEPT_BODY",BODY,{"disambiguationData":[OSD([sQuery(id+"F8.wireOp",EDGE,"E29")])]}),"instanceName":"3"});
            var Q21;
            Q21=makeQuery(id+"F10.opPattern","COPY",BODY,{"derivedFrom":makeQuery(id+"F9.opExtrude","SWEPT_BODY",BODY,{"disambiguationData":[OSD([sQuery(id+"F8.wireOp",EDGE,"E29")])]}),"instanceName":"4"});
            var Q22;
            Q22=makeQuery(id+"F10.opPattern","COPY",BODY,{"derivedFrom":makeQuery(id+"F9.opExtrude","SWEPT_BODY",BODY,{"disambiguationData":[OSD([sQuery(id+"F8.wireOp",EDGE,"E30")])]}),"instanceName":"3"});
            var Q23;
            Q23=makeQuery(id+"F10.opPattern","COPY",BODY,{"derivedFrom":makeQuery(id+"F9.opExtrude","SWEPT_BODY",BODY,{"disambiguationData":[OSD([sQuery(id+"F8.wireOp",EDGE,"E30")])]}),"instanceName":"4"});
            var Q24;
            Q24=makeQuery(id+"F10.opPattern","COPY",BODY,{"derivedFrom":makeQuery(id+"F9.opExtrude","SWEPT_BODY",BODY,{"disambiguationData":[OSD([sQuery(id+"F8.wireOp",EDGE,"E31")])]}),"instanceName":"6"});
            var Q25;
            Q25=makeQuery(id+"F10.opPattern","COPY",BODY,{"derivedFrom":makeQuery(id+"F9.opExtrude","SWEPT_BODY",BODY,{"disambiguationData":[OSD([sQuery(id+"F8.wireOp",EDGE,"E29")])]}),"instanceName":"6"});
            var Q26;
            Q26=makeQuery(id+"F10.opPattern","COPY",BODY,{"derivedFrom":makeQuery(id+"F9.opExtrude","SWEPT_BODY",BODY,{"disambiguationData":[OSD([sQuery(id+"F8.wireOp",EDGE,"E30")])]}),"instanceName":"6"});
            var Q27;
            Q27=makeQuery(id+"F10.opPattern","COPY",BODY,{"derivedFrom":makeQuery(id+"F9.opExtrude","SWEPT_BODY",BODY,{"disambiguationData":[OSD([sQuery(id+"F8.wireOp",EDGE,"E31")])]}),"instanceName":"7"});
            var Q28;
            Q28=makeQuery(id+"F10.opPattern","COPY",BODY,{"derivedFrom":makeQuery(id+"F9.opExtrude","SWEPT_BODY",BODY,{"disambiguationData":[OSD([sQuery(id+"F8.wireOp",EDGE,"E29")])]}),"instanceName":"7"});
            var Q29;
            Q29=makeQuery(id+"F10.opPattern","COPY",BODY,{"derivedFrom":makeQuery(id+"F9.opExtrude","SWEPT_BODY",BODY,{"disambiguationData":[OSD([sQuery(id+"F8.wireOp",EDGE,"E30")])]}),"instanceName":"7"});
            var Q30;
            Q30=makeQuery(id+"F10.opPattern","COPY",BODY,{"derivedFrom":makeQuery(id+"F9.opExtrude","SWEPT_BODY",BODY,{"disambiguationData":[OSD([sQuery(id+"F8.wireOp",EDGE,"E31")])]}),"instanceName":"8"});
            var Q31;
            Q31=makeQuery(id+"F10.opPattern","COPY",BODY,{"derivedFrom":makeQuery(id+"F9.opExtrude","SWEPT_BODY",BODY,{"disambiguationData":[OSD([sQuery(id+"F8.wireOp",EDGE,"E29")])]}),"instanceName":"8"});
            var Q32;
            Q32=makeQuery(id+"F10.opPattern","COPY",BODY,{"derivedFrom":makeQuery(id+"F9.opExtrude","SWEPT_BODY",BODY,{"disambiguationData":[OSD([sQuery(id+"F8.wireOp",EDGE,"E30")])]}),"instanceName":"8"});
            var Q33;
            Q33=makeQuery(id+"F10.opPattern","COPY",BODY,{"derivedFrom":makeQuery(id+"F9.opExtrude","SWEPT_BODY",BODY,{"disambiguationData":[OSD([sQuery(id+"F8.wireOp",EDGE,"E31")])]}),"instanceName":"9"});
            var Q34;
            Q34=makeQuery(id+"F10.opPattern","COPY",BODY,{"derivedFrom":makeQuery(id+"F9.opExtrude","SWEPT_BODY",BODY,{"disambiguationData":[OSD([sQuery(id+"F8.wireOp",EDGE,"E29")])]}),"instanceName":"9"});
            var Q35;
            Q35=makeQuery(id+"F10.opPattern","COPY",BODY,{"derivedFrom":makeQuery(id+"F9.opExtrude","SWEPT_BODY",BODY,{"disambiguationData":[OSD([sQuery(id+"F8.wireOp",EDGE,"E30")])]}),"instanceName":"9"});
            var Q36;
            Q36=makeQuery(id+"F10.opPattern","COPY",BODY,{"derivedFrom":makeQuery(id+"F9.opExtrude","SWEPT_BODY",BODY,{"disambiguationData":[OSD([sQuery(id+"F8.wireOp",EDGE,"E31")])]}),"instanceName":"10"});
            var Q37;
            Q37=makeQuery(id+"F10.opPattern","COPY",BODY,{"derivedFrom":makeQuery(id+"F9.opExtrude","SWEPT_BODY",BODY,{"disambiguationData":[OSD([sQuery(id+"F8.wireOp",EDGE,"E29")])]}),"instanceName":"10"});
            var Q38;
            Q38=makeQuery(id+"F10.opPattern","COPY",BODY,{"derivedFrom":makeQuery(id+"F9.opExtrude","SWEPT_BODY",BODY,{"disambiguationData":[OSD([sQuery(id+"F8.wireOp",EDGE,"E30")])]}),"instanceName":"10"});
            var Q39;
            Q39=makeQuery(id+"F10.opPattern","COPY",BODY,{"derivedFrom":makeQuery(id+"F9.opExtrude","SWEPT_BODY",BODY,{"disambiguationData":[OSD([sQuery(id+"F8.wireOp",EDGE,"E31")])]}),"instanceName":"11"});
            var Q40;
            Q40=makeQuery(id+"F10.opPattern","COPY",BODY,{"derivedFrom":makeQuery(id+"F9.opExtrude","SWEPT_BODY",BODY,{"disambiguationData":[OSD([sQuery(id+"F8.wireOp",EDGE,"E31")])]}),"instanceName":"12"});
            var Q41;
            Q41=makeQuery(id+"F10.opPattern","COPY",BODY,{"derivedFrom":makeQuery(id+"F9.opExtrude","SWEPT_BODY",BODY,{"disambiguationData":[OSD([sQuery(id+"F8.wireOp",EDGE,"E29")])]}),"instanceName":"11"});
            var Q42;
            Q42=makeQuery(id+"F10.opPattern","COPY",BODY,{"derivedFrom":makeQuery(id+"F9.opExtrude","SWEPT_BODY",BODY,{"disambiguationData":[OSD([sQuery(id+"F8.wireOp",EDGE,"E29")])]}),"instanceName":"12"});
            var Q43;
            Q43=makeQuery(id+"F10.opPattern","COPY",BODY,{"derivedFrom":makeQuery(id+"F9.opExtrude","SWEPT_BODY",BODY,{"disambiguationData":[OSD([sQuery(id+"F8.wireOp",EDGE,"E30")])]}),"instanceName":"11"});
            var Q44;
            Q44=makeQuery(id+"F10.opPattern","COPY",BODY,{"derivedFrom":makeQuery(id+"F9.opExtrude","SWEPT_BODY",BODY,{"disambiguationData":[OSD([sQuery(id+"F8.wireOp",EDGE,"E30")])]}),"instanceName":"12"});
            var Q45;
            Q45=makeQuery(id+"F10.opPattern","COPY",BODY,{"derivedFrom":makeQuery(id+"F9.opExtrude","SWEPT_BODY",BODY,{"disambiguationData":[OSD([sQuery(id+"F8.wireOp",EDGE,"E31")])]}),"instanceName":"13"});
            var Q46;
            Q46=makeQuery(id+"F10.opPattern","COPY",BODY,{"derivedFrom":makeQuery(id+"F9.opExtrude","SWEPT_BODY",BODY,{"disambiguationData":[OSD([sQuery(id+"F8.wireOp",EDGE,"E29")])]}),"instanceName":"13"});
            var Q47;
            Q47=makeQuery(id+"F10.opPattern","COPY",BODY,{"derivedFrom":makeQuery(id+"F9.opExtrude","SWEPT_BODY",BODY,{"disambiguationData":[OSD([sQuery(id+"F8.wireOp",EDGE,"E30")])]}),"instanceName":"13"});
            var Q48;
            Q48=makeQuery(id+"F3.opPattern","COPY",BODY,{"derivedFrom":makeQuery(id+"F1.opExtrude","SWEPT_BODY",BODY,{"disambiguationData":[OSD([sQuery(id+"F0.wireOp",EDGE,"E5"),sQuery(id+"F0.wireOp",EDGE,"E6"),sQuery(id+"F0.wireOp",EDGE,"E7"),sQuery(id+"F0.wireOp",EDGE,"E8")])]}),"instanceName":"9"});
            var Q49;
            Q49=makeQuery(id+"F3.opPattern","COPY",BODY,{"derivedFrom":makeQuery(id+"F1.opExtrude","SWEPT_BODY",BODY,{"disambiguationData":[OSD([sQuery(id+"F0.wireOp",EDGE,"E5"),sQuery(id+"F0.wireOp",EDGE,"E6"),sQuery(id+"F0.wireOp",EDGE,"E7"),sQuery(id+"F0.wireOp",EDGE,"E8")])]}),"instanceName":"8"});
            var Q50;
            Q50=makeQuery(id+"F3.opPattern","COPY",BODY,{"derivedFrom":makeQuery(id+"F1.opExtrude","SWEPT_BODY",BODY,{"disambiguationData":[OSD([sQuery(id+"F0.wireOp",EDGE,"E5"),sQuery(id+"F0.wireOp",EDGE,"E6"),sQuery(id+"F0.wireOp",EDGE,"E7"),sQuery(id+"F0.wireOp",EDGE,"E8")])]}),"instanceName":"7"});
            var Q51;
            Q51=makeQuery(id+"F3.opPattern","COPY",BODY,{"derivedFrom":makeQuery(id+"F1.opExtrude","SWEPT_BODY",BODY,{"disambiguationData":[OSD([sQuery(id+"F0.wireOp",EDGE,"E5"),sQuery(id+"F0.wireOp",EDGE,"E6"),sQuery(id+"F0.wireOp",EDGE,"E7"),sQuery(id+"F0.wireOp",EDGE,"E8")])]}),"instanceName":"6"});
            var Q52;
            Q52=makeQuery(id+"F3.opPattern","COPY",BODY,{"derivedFrom":makeQuery(id+"F1.opExtrude","SWEPT_BODY",BODY,{"disambiguationData":[OSD([sQuery(id+"F0.wireOp",EDGE,"E5"),sQuery(id+"F0.wireOp",EDGE,"E6"),sQuery(id+"F0.wireOp",EDGE,"E7"),sQuery(id+"F0.wireOp",EDGE,"E8")])]}),"instanceName":"5"});
            var Q53;
            Q53=makeQuery(id+"F3.opPattern","COPY",BODY,{"derivedFrom":makeQuery(id+"F1.opExtrude","SWEPT_BODY",BODY,{"disambiguationData":[OSD([sQuery(id+"F0.wireOp",EDGE,"E5"),sQuery(id+"F0.wireOp",EDGE,"E6"),sQuery(id+"F0.wireOp",EDGE,"E7"),sQuery(id+"F0.wireOp",EDGE,"E8")])]}),"instanceName":"4"});
            var Q54;
            Q54=makeQuery(id+"F3.opPattern","COPY",BODY,{"derivedFrom":makeQuery(id+"F1.opExtrude","SWEPT_BODY",BODY,{"disambiguationData":[OSD([sQuery(id+"F0.wireOp",EDGE,"E5"),sQuery(id+"F0.wireOp",EDGE,"E6"),sQuery(id+"F0.wireOp",EDGE,"E7"),sQuery(id+"F0.wireOp",EDGE,"E8")])]}),"instanceName":"3"});
            var Q55;
            Q55=makeQuery(id+"F3.opPattern","COPY",BODY,{"derivedFrom":makeQuery(id+"F1.opExtrude","SWEPT_BODY",BODY,{"disambiguationData":[OSD([sQuery(id+"F0.wireOp",EDGE,"E5"),sQuery(id+"F0.wireOp",EDGE,"E6"),sQuery(id+"F0.wireOp",EDGE,"E7"),sQuery(id+"F0.wireOp",EDGE,"E8")])]}),"instanceName":"2"});
            var Q56;
            Q56=makeQuery(id+"F3.opPattern","COPY",BODY,{"derivedFrom":makeQuery(id+"F1.opExtrude","SWEPT_BODY",BODY,{"disambiguationData":[OSD([sQuery(id+"F0.wireOp",EDGE,"E5"),sQuery(id+"F0.wireOp",EDGE,"E6"),sQuery(id+"F0.wireOp",EDGE,"E7"),sQuery(id+"F0.wireOp",EDGE,"E8")])]}),"instanceName":"1"});
            var Q57;
            Q57=makeQuery(id+"F1.opExtrude","SWEPT_BODY",BODY,{"disambiguationData":[OSD([sQuery(id+"F0.wireOp",EDGE,"E5"),sQuery(id+"F0.wireOp",EDGE,"E6"),sQuery(id+"F0.wireOp",EDGE,"E7"),sQuery(id+"F0.wireOp",EDGE,"E8")])]});
            var Q58;
            Q58=makeQuery(id+"F3.opPattern","COPY",BODY,{"derivedFrom":makeQuery(id+"F1.opExtrude","SWEPT_BODY",BODY,{"disambiguationData":[OSD([sQuery(id+"F0.wireOp",EDGE,"E5"),sQuery(id+"F0.wireOp",EDGE,"E6"),sQuery(id+"F0.wireOp",EDGE,"E7"),sQuery(id+"F0.wireOp",EDGE,"E8")])]}),"instanceName":"15"});
            var Q59;
            Q59=makeQuery(id+"F3.opPattern","COPY",BODY,{"derivedFrom":makeQuery(id+"F1.opExtrude","SWEPT_BODY",BODY,{"disambiguationData":[OSD([sQuery(id+"F0.wireOp",EDGE,"E5"),sQuery(id+"F0.wireOp",EDGE,"E6"),sQuery(id+"F0.wireOp",EDGE,"E7"),sQuery(id+"F0.wireOp",EDGE,"E8")])]}),"instanceName":"14"});
            var Q60;
            Q60=makeQuery(id+"F3.opPattern","COPY",BODY,{"derivedFrom":makeQuery(id+"F1.opExtrude","SWEPT_BODY",BODY,{"disambiguationData":[OSD([sQuery(id+"F0.wireOp",EDGE,"E5"),sQuery(id+"F0.wireOp",EDGE,"E6"),sQuery(id+"F0.wireOp",EDGE,"E7"),sQuery(id+"F0.wireOp",EDGE,"E8")])]}),"instanceName":"13"});
            var Q61;
            Q61=makeQuery(id+"F3.opPattern","COPY",BODY,{"derivedFrom":makeQuery(id+"F1.opExtrude","SWEPT_BODY",BODY,{"disambiguationData":[OSD([sQuery(id+"F0.wireOp",EDGE,"E5"),sQuery(id+"F0.wireOp",EDGE,"E6"),sQuery(id+"F0.wireOp",EDGE,"E7"),sQuery(id+"F0.wireOp",EDGE,"E8")])]}),"instanceName":"12"});
            var Q62;
            Q62=makeQuery(id+"F3.opPattern","COPY",BODY,{"derivedFrom":makeQuery(id+"F1.opExtrude","SWEPT_BODY",BODY,{"disambiguationData":[OSD([sQuery(id+"F0.wireOp",EDGE,"E5"),sQuery(id+"F0.wireOp",EDGE,"E6"),sQuery(id+"F0.wireOp",EDGE,"E7"),sQuery(id+"F0.wireOp",EDGE,"E8")])]}),"instanceName":"11"});
            var Q63;
            Q63=makeQuery(id+"F3.opPattern","COPY",BODY,{"derivedFrom":makeQuery(id+"F1.opExtrude","SWEPT_BODY",BODY,{"disambiguationData":[OSD([sQuery(id+"F0.wireOp",EDGE,"E5"),sQuery(id+"F0.wireOp",EDGE,"E6"),sQuery(id+"F0.wireOp",EDGE,"E7"),sQuery(id+"F0.wireOp",EDGE,"E8")])]}),"instanceName":"10"});
            booleanBodies(context, id + "F11", {"operationType" : BooleanOperationType.SUBTRACTION, "tools" : qUnion([Q0, Q1, Q2, Q3, Q4, Q5, Q6, Q7, Q8, Q9, Q10, Q11, Q12, Q13, Q14, Q15, Q16, Q17, Q18, Q19, Q20, Q21, Q22, Q23, Q24, Q25, Q26, Q27, Q28, Q29, Q30, Q31, Q32, Q33, Q34, Q35, Q36, Q37, Q38, Q39, Q40, Q41, Q42, Q43, Q44, Q45, Q46, Q47]), "targets" : qUnion([Q48, Q49, Q50, Q51, Q52, Q53, Q54, Q55, Q56, Q57, Q58, Q59, Q60, Q61, Q62, Q63])});
        }
    });
